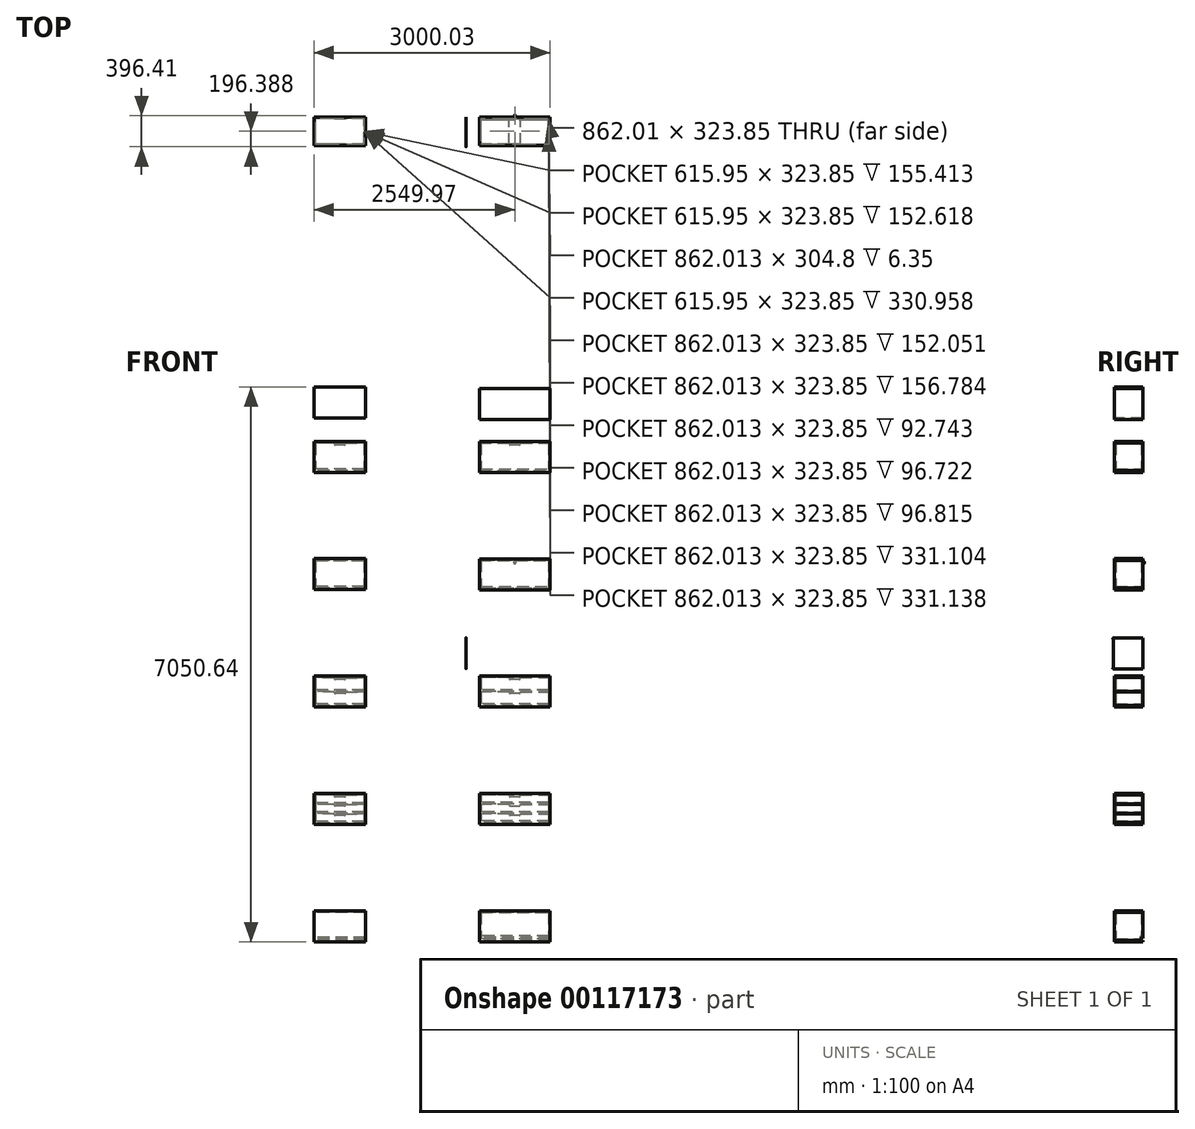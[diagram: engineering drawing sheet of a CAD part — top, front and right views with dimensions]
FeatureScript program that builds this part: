
annotation { "Feature Type Name" : "Feature", "Feature Type Description" : "" }
export const myFeature = defineFeature(function(context is Context, id is Id, definition is map)
    precondition{}
    {
        {
            var Q0;
            Q0=qCreatedBy(makeId("Front.planeOp"),FACE);
            var sketch = newSketch(context, id + "F0", { "sketchPlane" : qUnion([Q0])});
            skLineSegment(sketch, "E0", {"start": v(170.28, 4762.46) * mm, "end": v(167.36, 4762.46) * mm});
            skLineSegment(sketch, "E1", {"start": v(170.28, 4769.46) * mm, "end": v(167.36, 4769.46) * mm});
            skLineSegment(sketch, "E2", {"start": v(167.36, 4391.46) * mm, "end": v(170.28, 4391.46) * mm});
            skLineSegment(sketch, "E3", {"start": v(167.36, 4391.46) * mm, "end": v(167.36, 4769.46) * mm});
            skLineSegment(sketch, "E4", {"start": v(170.28, 4391.46) * mm, "end": v(170.28, 4769.46) * mm});
            skLineSegment(sketch, "E5", {"start": v(170.28, 3279.46) * mm, "end": v(167.36, 3279.46) * mm});
            skLineSegment(sketch, "E6", {"start": v(1435.25, 5048.46) * mm, "end": v(1435.25, 5411.54) * mm});
            skLineSegment(sketch, "E7", {"start": v(170.32, 5032.75) * mm, "end": v(170.32, 5427.25) * mm});
            skLineSegment(sketch, "E8", {"start": v(167.32, 5427.25) * mm, "end": v(167.32, 5032.75) * mm});
            skLineSegment(sketch, "E9", {"start": v(1070.32, 5032.75) * mm, "end": v(1070.32, 5427.25) * mm});
            skLineSegment(sketch, "E10", {"start": v(1073.32, 5427.25) * mm, "end": v(1073.32, 5032.75) * mm});
            skLineSegment(sketch, "E11", {"start": v(1809.25, 3937.25) * mm, "end": v(1809.25, 3542.75) * mm});
            skLineSegment(sketch, "E12", {"start": v(1809.25, 5427.25) * mm, "end": v(1809.25, 5032.75) * mm});
            skLineSegment(sketch, "E13", {"start": v(167.32, 3930.25) * mm, "end": v(170.32, 3930.25) * mm});
            skLineSegment(sketch, "E14", {"start": v(167.32, 5032.75) * mm, "end": v(170.32, 5032.75) * mm});
            skLineSegment(sketch, "E15", {"start": v(1073.32, 5032.75) * mm, "end": v(1070.32, 5032.75) * mm});
            skLineSegment(sketch, "E16", {"start": v(170.32, 5032.75) * mm, "end": v(1070.32, 5032.75) * mm});
            skLineSegment(sketch, "E17", {"start": v(1070.32, 5051.75) * mm, "end": v(170.32, 5051.75) * mm});
            skLineSegment(sketch, "E18", {"start": v(170.28, 4391.46) * mm, "end": v(1070.36, 4391.46) * mm});
            skLineSegment(sketch, "E19", {"start": v(170.28, 4747.46) * mm, "end": v(1070.36, 4747.46) * mm});
            skLineSegment(sketch, "E20", {"start": v(1073.28, 4391.46) * mm, "end": v(1070.36, 4391.46) * mm});
            skLineSegment(sketch, "E21", {"start": v(1073.28, 4391.46) * mm, "end": v(1073.28, 4769.46) * mm});
            skLineSegment(sketch, "E22", {"start": v(1070.36, 4391.46) * mm, "end": v(1070.36, 4769.46) * mm});
            skLineSegment(sketch, "E23", {"start": v(1070.36, 4769.46) * mm, "end": v(1073.28, 4769.46) * mm});
            skLineSegment(sketch, "E24", {"start": v(1070.36, 4762.46) * mm, "end": v(1073.28, 4762.46) * mm});
            skLineSegment(sketch, "E25", {"start": v(170.32, 3918.25) * mm, "end": v(1070.32, 3918.25) * mm});
            skLineSegment(sketch, "E26", {"start": v(1070.32, 3561.75) * mm, "end": v(170.32, 3561.75) * mm});
            skLineSegment(sketch, "E27", {"start": v(170.32, 3542.75) * mm, "end": v(1070.32, 3542.75) * mm});
            skLineSegment(sketch, "E28", {"start": v(170.32, 3937.25) * mm, "end": v(1070.32, 3937.25) * mm});
            skLineSegment(sketch, "E29", {"start": v(1073.32, 3937.25) * mm, "end": v(1073.32, 3542.75) * mm});
            skLineSegment(sketch, "E30", {"start": v(1070.32, 3542.75) * mm, "end": v(1070.32, 3937.25) * mm});
            skLineSegment(sketch, "E31", {"start": v(1073.32, 3542.75) * mm, "end": v(1070.32, 3542.75) * mm});
            skLineSegment(sketch, "E32", {"start": v(1073.32, 3937.25) * mm, "end": v(1070.32, 3937.25) * mm});
            skLineSegment(sketch, "E33", {"start": v(1073.32, 3930.25) * mm, "end": v(1070.32, 3930.25) * mm});
            skLineSegment(sketch, "E34", {"start": v(170.28, 3257.46) * mm, "end": v(1070.36, 3257.46) * mm});
            skLineSegment(sketch, "E35", {"start": v(1070.36, 3279.46) * mm, "end": v(1073.28, 3279.46) * mm});
            skLineSegment(sketch, "E36", {"start": v(1070.36, 3272.46) * mm, "end": v(1073.28, 3272.46) * mm});
            skLineSegment(sketch, "E37", {"start": v(170.28, 3272.46) * mm, "end": v(167.36, 3272.46) * mm});
            skLineSegment(sketch, "E38", {"start": v(1073.32, 5427.25) * mm, "end": v(1070.32, 5427.25) * mm});
            skLineSegment(sketch, "E39", {"start": v(170.32, 5427.25) * mm, "end": v(1070.32, 5427.25) * mm});
            skLineSegment(sketch, "E40", {"start": v(170.32, 5408.25) * mm, "end": v(1070.32, 5408.25) * mm});
            skCircle(sketch, "E41", {"center": v(1439.75, 5041.25) * mm, "radius": 4 * mm});
            skEllipticalArc(sketch, "E42", {});
            skCircle(sketch, "E43", {"center": v(1439.75, 3928.75) * mm, "radius": 4 * mm});
            skEllipticalArc(sketch, "E44", {});
            skCircle(sketch, "E45", {"center": v(1439.75, 3551.25) * mm, "radius": 4 * mm});
            skEllipticalArc(sketch, "E46", {});
            skLineSegment(sketch, "E47", {"start": v(1435.25, 3558.46) * mm, "end": v(1435.25, 3921.54) * mm});
            skCircle(sketch, "E48", {"center": v(620.36, 3888.25) * mm, "radius": 13 * mm});
            skCircle(sketch, "E49", {"center": v(620.36, 3888.25) * mm, "radius": 14 * mm});
            skLineSegment(sketch, "E50", {"start": v(621.1, 3893.25) * mm, "end": v(621.1, 3883.25) * mm});
            skLineSegment(sketch, "E51", {"start": v(621.1, 3883.25) * mm, "end": v(619.6, 3883.25) * mm});
            skLineSegment(sketch, "E52", {"start": v(619.6, 3883.25) * mm, "end": v(619.6, 3893.25) * mm});
            skLineSegment(sketch, "E53", {"start": v(621.1, 3893.25) * mm, "end": v(619.6, 3893.25) * mm});
            skLineSegment(sketch, "E54", {"start": v(170.32, 3542.75) * mm, "end": v(170.32, 3937.25) * mm});
            skLineSegment(sketch, "E55", {"start": v(167.32, 3937.25) * mm, "end": v(167.32, 3542.75) * mm});
            skLineSegment(sketch, "E56", {"start": v(167.32, 3542.75) * mm, "end": v(170.32, 3542.75) * mm});
            skLineSegment(sketch, "E57", {"start": v(167.32, 3937.25) * mm, "end": v(170.32, 3937.25) * mm});
            skLineSegment(sketch, "E58", {"start": v(170.28, 277.46) * mm, "end": v(1070.36, 277.46) * mm});
            skLineSegment(sketch, "E59", {"start": v(1070.36, 299.46) * mm, "end": v(1073.28, 299.46) * mm});
            skLineSegment(sketch, "E60", {"start": v(1070.36, 292.46) * mm, "end": v(1073.28, 292.46) * mm});
            skLineSegment(sketch, "E61", {"start": v(170.28, 292.46) * mm, "end": v(167.36, 292.46) * mm});
            skLineSegment(sketch, "E62", {"start": v(170.28, 1782.46) * mm, "end": v(167.36, 1782.46) * mm});
            skLineSegment(sketch, "E63", {"start": v(167.36, 1411.46) * mm, "end": v(170.28, 1411.46) * mm});
            skLineSegment(sketch, "E64", {"start": v(167.36, 1411.46) * mm, "end": v(167.36, 1789.46) * mm});
            skLineSegment(sketch, "E65", {"start": v(170.28, 1411.46) * mm, "end": v(170.28, 1789.46) * mm});
            skLineSegment(sketch, "E66", {"start": v(170.28, 299.46) * mm, "end": v(167.36, 299.46) * mm});
            skLineSegment(sketch, "E67", {"start": v(170.28, 1789.46) * mm, "end": v(167.36, 1789.46) * mm});
            skLineSegment(sketch, "E68", {"start": v(1809.25, 2447.25) * mm, "end": v(1809.25, 2052.75) * mm});
            skLineSegment(sketch, "E69", {"start": v(1809.25, 957.25) * mm, "end": v(1809.25, 562.75) * mm});
            skCircle(sketch, "E70", {"center": v(1439.75, 5418.75) * mm, "radius": 4 * mm});
            skEllipticalArc(sketch, "E71", {});
            skArc(sketch, "E72", {"start": v(548.59, 5408.25) * mm, "mid": v(550.53, 5407.44) * mm, "end": v(551.34, 5405.5) * mm});
            skLineSegment(sketch, "E73", {"start": v(560.34, 5382.25) * mm, "end": v(680.34, 5382.25) * mm});
            skArc(sketch, "E74", {"start": v(551.34, 5391.25) * mm, "mid": v(553.97, 5384.88) * mm, "end": v(560.34, 5382.25) * mm});
            skArc(sketch, "E75", {"start": v(680.34, 5382.25) * mm, "mid": v(686.7, 5384.88) * mm, "end": v(689.34, 5391.25) * mm});
            skArc(sketch, "E76", {"start": v(692.09, 5408.25) * mm, "mid": v(690.14, 5407.44) * mm, "end": v(689.34, 5405.5) * mm});
            skLineSegment(sketch, "E77", {"start": v(551.34, 5405.5) * mm, "end": v(551.34, 5391.25) * mm});
            skLineSegment(sketch, "E78", {"start": v(689.34, 5405.5) * mm, "end": v(689.34, 5391.25) * mm});
            skLineSegment(sketch, "E79", {"start": v(167.32, 5427.25) * mm, "end": v(170.32, 5427.25) * mm});
            skLineSegment(sketch, "E80", {"start": v(167.32, 5420.25) * mm, "end": v(170.32, 5420.25) * mm});
            skLineSegment(sketch, "E81", {"start": v(1073.32, 5420.25) * mm, "end": v(1070.32, 5420.25) * mm});
            skLineSegment(sketch, "E82", {"start": v(170.32, 2447.25) * mm, "end": v(1070.32, 2447.25) * mm});
            skLineSegment(sketch, "E83", {"start": v(170.32, 2250) * mm, "end": v(1070.32, 2250) * mm});
            skLineSegment(sketch, "E84", {"start": v(1073.32, 2447.25) * mm, "end": v(1073.32, 2052.75) * mm});
            skLineSegment(sketch, "E85", {"start": v(1070.32, 2052.75) * mm, "end": v(1070.32, 2447.25) * mm});
            skLineSegment(sketch, "E86", {"start": v(1073.32, 2052.75) * mm, "end": v(1070.32, 2052.75) * mm});
            skLineSegment(sketch, "E87", {"start": v(1073.32, 2447.25) * mm, "end": v(1070.32, 2447.25) * mm});
            skLineSegment(sketch, "E88", {"start": v(1073.32, 2440.25) * mm, "end": v(1070.32, 2440.25) * mm});
            skLineSegment(sketch, "E89", {"start": v(170.28, 1767.46) * mm, "end": v(1070.36, 1767.46) * mm});
            skLineSegment(sketch, "E90", {"start": v(170.28, 1411.46) * mm, "end": v(1070.36, 1411.46) * mm});
            skLineSegment(sketch, "E91", {"start": v(1073.28, 1411.46) * mm, "end": v(1073.28, 1789.46) * mm});
            skLineSegment(sketch, "E92", {"start": v(1070.36, 1411.46) * mm, "end": v(1070.36, 1789.46) * mm});
            skLineSegment(sketch, "E93", {"start": v(1073.28, 1411.46) * mm, "end": v(1070.36, 1411.46) * mm});
            skLineSegment(sketch, "E94", {"start": v(1070.36, 1789.46) * mm, "end": v(1073.28, 1789.46) * mm});
            skLineSegment(sketch, "E95", {"start": v(1070.36, 1782.46) * mm, "end": v(1073.28, 1782.46) * mm});
            skLineSegment(sketch, "E96", {"start": v(170.32, 957.25) * mm, "end": v(1070.32, 957.25) * mm});
            skLineSegment(sketch, "E97", {"start": v(170.32, 938.25) * mm, "end": v(1070.32, 938.25) * mm});
            skLineSegment(sketch, "E98", {"start": v(1070.32, 581.75) * mm, "end": v(170.32, 581.75) * mm});
            skLineSegment(sketch, "E99", {"start": v(170.32, 562.75) * mm, "end": v(1070.32, 562.75) * mm});
            skLineSegment(sketch, "E100", {"start": v(170.32, 700.58) * mm, "end": v(1070.32, 700.58) * mm});
            skLineSegment(sketch, "E101", {"start": v(170.32, 819.4) * mm, "end": v(1070.32, 819.4) * mm});
            skLineSegment(sketch, "E102", {"start": v(1073.32, 957.25) * mm, "end": v(1070.32, 957.25) * mm});
            skLineSegment(sketch, "E103", {"start": v(1073.32, 957.25) * mm, "end": v(1073.32, 562.75) * mm});
            skLineSegment(sketch, "E104", {"start": v(1070.32, 562.75) * mm, "end": v(1070.32, 957.25) * mm});
            skLineSegment(sketch, "E105", {"start": v(1073.32, 562.75) * mm, "end": v(1070.32, 562.75) * mm});
            skLineSegment(sketch, "E106", {"start": v(1073.32, 950.25) * mm, "end": v(1070.32, 950.25) * mm});
            skArc(sketch, "E107", {"start": v(692.09, 2250) * mm, "mid": v(690.14, 2249.2) * mm, "end": v(689.34, 2247.25) * mm});
            skLineSegment(sketch, "E108", {"start": v(551.34, 2247.25) * mm, "end": v(551.34, 2233) * mm});
            skLineSegment(sketch, "E109", {"start": v(689.34, 2247.25) * mm, "end": v(689.34, 2233) * mm});
            skArc(sketch, "E110", {"start": v(548.59, 2250) * mm, "mid": v(550.53, 2249.2) * mm, "end": v(551.34, 2247.25) * mm});
            skArc(sketch, "E111", {"start": v(680.34, 2224) * mm, "mid": v(686.7, 2226.63) * mm, "end": v(689.34, 2233) * mm});
            skArc(sketch, "E112", {"start": v(692.09, 938.25) * mm, "mid": v(690.14, 937.44) * mm, "end": v(689.34, 935.5) * mm});
            skLineSegment(sketch, "E113", {"start": v(560.34, 912.25) * mm, "end": v(680.34, 912.25) * mm});
            skArc(sketch, "E114", {"start": v(680.34, 912.25) * mm, "mid": v(686.7, 914.88) * mm, "end": v(689.34, 921.25) * mm});
            skArc(sketch, "E115", {"start": v(551.34, 921.25) * mm, "mid": v(553.97, 914.88) * mm, "end": v(560.34, 912.25) * mm});
            skArc(sketch, "E116", {"start": v(692.09, 819.4) * mm, "mid": v(690.14, 818.6) * mm, "end": v(689.34, 816.66) * mm});
            skArc(sketch, "E117", {"start": v(548.59, 700.58) * mm, "mid": v(550.53, 699.77) * mm, "end": v(551.34, 697.83) * mm});
            skLineSegment(sketch, "E118", {"start": v(689.34, 697.83) * mm, "end": v(689.34, 683.58) * mm});
            skLineSegment(sketch, "E119", {"start": v(170.32, 562.75) * mm, "end": v(170.32, 957.25) * mm});
            skLineSegment(sketch, "E120", {"start": v(167.32, 957.25) * mm, "end": v(167.32, 562.75) * mm});
            skLineSegment(sketch, "E121", {"start": v(167.32, 562.75) * mm, "end": v(170.32, 562.75) * mm});
            skLineSegment(sketch, "E122", {"start": v(167.32, 957.25) * mm, "end": v(170.32, 957.25) * mm});
            skLineSegment(sketch, "E123", {"start": v(167.32, 950.25) * mm, "end": v(170.32, 950.25) * mm});
            skLineSegment(sketch, "E124", {"start": v(170.32, 2052.75) * mm, "end": v(170.32, 2447.25) * mm});
            skLineSegment(sketch, "E125", {"start": v(167.32, 2447.25) * mm, "end": v(167.32, 2052.75) * mm});
            skLineSegment(sketch, "E126", {"start": v(167.32, 2052.75) * mm, "end": v(170.32, 2052.75) * mm});
            skLineSegment(sketch, "E127", {"start": v(167.32, 2447.25) * mm, "end": v(170.32, 2447.25) * mm});
            skLineSegment(sketch, "E128", {"start": v(167.32, 2440.25) * mm, "end": v(170.32, 2440.25) * mm});
            skLineSegment(sketch, "E129", {"start": v(170.32, 2428.25) * mm, "end": v(1070.32, 2428.25) * mm});
            skLineSegment(sketch, "E130", {"start": v(1070.32, 2071.75) * mm, "end": v(170.32, 2071.75) * mm});
            skLineSegment(sketch, "E131", {"start": v(170.32, 2052.75) * mm, "end": v(1070.32, 2052.75) * mm});
            skEllipticalArc(sketch, "E132", {});
            skLineSegment(sketch, "E133", {"start": v(1435.25, 578.46) * mm, "end": v(1435.25, 941.54) * mm});
            skLineSegment(sketch, "E134", {"start": v(551.34, 816.66) * mm, "end": v(551.34, 802.4) * mm});
            skArc(sketch, "E135", {"start": v(548.59, 938.25) * mm, "mid": v(550.53, 937.44) * mm, "end": v(551.34, 935.5) * mm});
            skLineSegment(sketch, "E136", {"start": v(689.34, 935.5) * mm, "end": v(689.34, 921.25) * mm});
            skLineSegment(sketch, "E137", {"start": v(551.34, 935.5) * mm, "end": v(551.34, 921.25) * mm});
            skLineSegment(sketch, "E138", {"start": v(551.34, 697.83) * mm, "end": v(551.34, 683.58) * mm});
            skArc(sketch, "E139", {"start": v(692.09, 700.58) * mm, "mid": v(690.14, 699.77) * mm, "end": v(689.34, 697.83) * mm});
            skLineSegment(sketch, "E140", {"start": v(560.34, 674.58) * mm, "end": v(680.34, 674.58) * mm});
            skArc(sketch, "E141", {"start": v(680.34, 674.58) * mm, "mid": v(686.7, 677.21) * mm, "end": v(689.34, 683.58) * mm});
            skArc(sketch, "E142", {"start": v(551.34, 683.58) * mm, "mid": v(553.97, 677.21) * mm, "end": v(560.34, 674.58) * mm});
            skArc(sketch, "E143", {"start": v(551.34, 802.4) * mm, "mid": v(553.97, 796.04) * mm, "end": v(560.34, 793.4) * mm});
            skArc(sketch, "E144", {"start": v(680.34, 793.4) * mm, "mid": v(686.7, 796.04) * mm, "end": v(689.34, 802.4) * mm});
            skLineSegment(sketch, "E145", {"start": v(560.34, 793.4) * mm, "end": v(680.34, 793.4) * mm});
            skLineSegment(sketch, "E146", {"start": v(689.34, 816.66) * mm, "end": v(689.34, 802.4) * mm});
            skArc(sketch, "E147", {"start": v(548.59, 819.4) * mm, "mid": v(550.53, 818.6) * mm, "end": v(551.34, 816.66) * mm});
            skArc(sketch, "E148", {"start": v(548.59, 2428.25) * mm, "mid": v(550.53, 2427.44) * mm, "end": v(551.34, 2425.5) * mm});
            skLineSegment(sketch, "E149", {"start": v(689.34, 2425.5) * mm, "end": v(689.34, 2411.25) * mm});
            skLineSegment(sketch, "E150", {"start": v(551.34, 2425.5) * mm, "end": v(551.34, 2411.25) * mm});
            skArc(sketch, "E151", {"start": v(692.09, 2428.25) * mm, "mid": v(690.14, 2427.44) * mm, "end": v(689.34, 2425.5) * mm});
            skLineSegment(sketch, "E152", {"start": v(560.34, 2402.25) * mm, "end": v(680.34, 2402.25) * mm});
            skArc(sketch, "E153", {"start": v(680.34, 2402.25) * mm, "mid": v(686.7, 2404.88) * mm, "end": v(689.34, 2411.25) * mm});
            skArc(sketch, "E154", {"start": v(551.34, 2411.25) * mm, "mid": v(553.97, 2404.88) * mm, "end": v(560.34, 2402.25) * mm});
            skArc(sketch, "E155", {"start": v(551.34, 2233) * mm, "mid": v(553.97, 2226.63) * mm, "end": v(560.34, 2224) * mm});
            skLineSegment(sketch, "E156", {"start": v(560.34, 2224) * mm, "end": v(680.34, 2224) * mm});
            skLineSegment(sketch, "E157", {"start": v(-1274.6, 4769.46) * mm, "end": v(-1271.68, 4769.46) * mm});
            skLineSegment(sketch, "E158", {"start": v(-1271.68, 4391.46) * mm, "end": v(-1274.6, 4391.46) * mm});
            skLineSegment(sketch, "E159", {"start": v(-1274.6, 4391.46) * mm, "end": v(-1274.6, 4769.46) * mm});
            skLineSegment(sketch, "E160", {"start": v(-1271.68, 4391.46) * mm, "end": v(-1271.68, 4769.46) * mm});
            skLineSegment(sketch, "E161", {"start": v(-1274.6, 4762.46) * mm, "end": v(-1271.68, 4762.46) * mm});
            skLineSegment(sketch, "E162", {"start": v(-1274.6, 3279.46) * mm, "end": v(-1271.68, 3279.46) * mm});
            skLineSegment(sketch, "E163", {"start": v(-1274.6, 3272.46) * mm, "end": v(-1271.68, 3272.46) * mm});
            skLineSegment(sketch, "E164", {"start": v(-664.75, 5048.46) * mm, "end": v(-664.75, 5411.54) * mm});
            skLineSegment(sketch, "E165", {"start": v(-290.75, 5427.25) * mm, "end": v(-290.75, 5032.75) * mm});
            skLineSegment(sketch, "E166", {"start": v(-1271.64, 5427.25) * mm, "end": v(-1271.64, 5032.75) * mm});
            skLineSegment(sketch, "E167", {"start": v(-1274.64, 5032.75) * mm, "end": v(-1274.64, 5427.25) * mm});
            skCircle(sketch, "E168", {"center": v(1439.75, 2438.75) * mm, "radius": 4 * mm});
            skEllipticalArc(sketch, "E169", {});
            skCircle(sketch, "E170", {"center": v(1439.75, 2061.25) * mm, "radius": 4 * mm});
            skEllipticalArc(sketch, "E171", {});
            skLineSegment(sketch, "E172", {"start": v(1435.25, 2068.46) * mm, "end": v(1435.25, 2431.54) * mm});
            skCircle(sketch, "E173", {"center": v(1439.75, 948.75) * mm, "radius": 4 * mm});
            skEllipticalArc(sketch, "E174", {});
            skCircle(sketch, "E175", {"center": v(1439.75, 571.25) * mm, "radius": 4 * mm});
            skLineSegment(sketch, "E176", {"start": v(-1929.64, 5032.75) * mm, "end": v(-1929.64, 5427.25) * mm});
            skLineSegment(sketch, "E177", {"start": v(-1271.64, 5420.25) * mm, "end": v(-1274.64, 5420.25) * mm});
            skLineSegment(sketch, "E178", {"start": v(-660.25, 5427.25) * mm, "end": v(-290.75, 5427.25) * mm});
            skCircle(sketch, "E179", {"center": v(-660.25, 5418.75) * mm, "radius": 4 * mm});
            skEllipticalArc(sketch, "E180", {});
            skLineSegment(sketch, "E181", {"start": v(-1271.64, 5427.25) * mm, "end": v(-1274.64, 5427.25) * mm});
            skLineSegment(sketch, "E182", {"start": v(-1271.64, 3930.25) * mm, "end": v(-1274.64, 3930.25) * mm});
            skCircle(sketch, "E183", {"center": v(-660.25, 5041.25) * mm, "radius": 4 * mm});
            skEllipticalArc(sketch, "E184", {});
            skLineSegment(sketch, "E185", {"start": v(-660.61, 5032.75) * mm, "end": v(-290.75, 5032.75) * mm});
            skCircle(sketch, "E186", {"center": v(-660.25, 3928.75) * mm, "radius": 4 * mm});
            skEllipticalArc(sketch, "E187", {});
            skLineSegment(sketch, "E188", {"start": v(-660.25, 3937.25) * mm, "end": v(-290.75, 3937.25) * mm});
            skCircle(sketch, "E189", {"center": v(-660.25, 3551.25) * mm, "radius": 4 * mm});
            skEllipticalArc(sketch, "E190", {});
            skLineSegment(sketch, "E191", {"start": v(-660.61, 3542.75) * mm, "end": v(-290.75, 3542.75) * mm});
            skLineSegment(sketch, "E192", {"start": v(-664.75, 3558.46) * mm, "end": v(-664.75, 3921.54) * mm});
            skLineSegment(sketch, "E193", {"start": v(-290.75, 3937.25) * mm, "end": v(-290.75, 3542.75) * mm});
            skLineSegment(sketch, "E194", {"start": v(-1274.64, 3542.75) * mm, "end": v(-1274.64, 3937.25) * mm});
            skLineSegment(sketch, "E195", {"start": v(-1271.64, 3542.75) * mm, "end": v(-1274.64, 3542.75) * mm});
            skLineSegment(sketch, "E196", {"start": v(-1271.64, 3937.25) * mm, "end": v(-1274.64, 3937.25) * mm});
            skLineSegment(sketch, "E197", {"start": v(-1271.64, 3937.25) * mm, "end": v(-1271.64, 3542.75) * mm});
            skLineSegment(sketch, "E198", {"start": v(-1271.64, 5032.75) * mm, "end": v(-1274.64, 5032.75) * mm});
            skLineSegment(sketch, "E199", {"start": v(-1671.16, 5405.5) * mm, "end": v(-1671.16, 5391.25) * mm});
            skLineSegment(sketch, "E200", {"start": v(-1932.64, 3930.25) * mm, "end": v(-1929.64, 3930.25) * mm});
            skLineSegment(sketch, "E201", {"start": v(-1932.64, 5032.75) * mm, "end": v(-1929.64, 5032.75) * mm});
            skLineSegment(sketch, "E202", {"start": v(-1932.64, 3937.25) * mm, "end": v(-1929.64, 3937.25) * mm});
            skLineSegment(sketch, "E203", {"start": v(-1932.64, 3542.75) * mm, "end": v(-1929.64, 3542.75) * mm});
            skLineSegment(sketch, "E204", {"start": v(-1932.64, 3937.25) * mm, "end": v(-1932.64, 3542.75) * mm});
            skLineSegment(sketch, "E205", {"start": v(-1929.64, 3542.75) * mm, "end": v(-1929.64, 3937.25) * mm});
            skLineSegment(sketch, "E206", {"start": v(-1929.68, 3279.46) * mm, "end": v(-1932.6, 3279.46) * mm});
            skLineSegment(sketch, "E207", {"start": v(-1929.68, 3272.46) * mm, "end": v(-1932.6, 3272.46) * mm});
            skLineSegment(sketch, "E208", {"start": v(-1929.68, 4391.46) * mm, "end": v(-1929.68, 4769.46) * mm});
            skLineSegment(sketch, "E209", {"start": v(-1932.6, 4391.46) * mm, "end": v(-1932.6, 4769.46) * mm});
            skLineSegment(sketch, "E210", {"start": v(-1932.6, 4391.46) * mm, "end": v(-1929.68, 4391.46) * mm});
            skLineSegment(sketch, "E211", {"start": v(-1929.68, 4769.46) * mm, "end": v(-1932.6, 4769.46) * mm});
            skLineSegment(sketch, "E212", {"start": v(-1929.68, 4762.46) * mm, "end": v(-1932.6, 4762.46) * mm});
            skCircle(sketch, "E213", {"center": v(-1602.14, 3888.25) * mm, "radius": 13 * mm});
            skCircle(sketch, "E214", {"center": v(-1602.14, 3888.25) * mm, "radius": 14 * mm});
            skLineSegment(sketch, "E215", {"start": v(-1602.9, 3883.25) * mm, "end": v(-1602.9, 3893.25) * mm});
            skLineSegment(sketch, "E216", {"start": v(-1601.4, 3893.25) * mm, "end": v(-1602.9, 3893.25) * mm});
            skLineSegment(sketch, "E217", {"start": v(-1601.4, 3883.25) * mm, "end": v(-1602.9, 3883.25) * mm});
            skLineSegment(sketch, "E218", {"start": v(-1601.4, 3893.25) * mm, "end": v(-1601.4, 3883.25) * mm});
            skLineSegment(sketch, "E219", {"start": v(-1932.64, 5427.25) * mm, "end": v(-1932.64, 5032.75) * mm});
            skLineSegment(sketch, "E220", {"start": v(-660.61, 562.75) * mm, "end": v(-290.75, 562.75) * mm});
            skLineSegment(sketch, "E221", {"start": v(-664.75, 578.46) * mm, "end": v(-664.75, 941.54) * mm});
            skLineSegment(sketch, "E222", {"start": v(-290.75, 957.25) * mm, "end": v(-290.75, 562.75) * mm});
            skCircle(sketch, "E223", {"center": v(-660.25, 948.75) * mm, "radius": 4 * mm});
            skCircle(sketch, "E224", {"center": v(-660.25, 2438.75) * mm, "radius": 4 * mm});
            skEllipticalArc(sketch, "E225", {});
            skLineSegment(sketch, "E226", {"start": v(-1271.64, 957.25) * mm, "end": v(-1271.64, 562.75) * mm});
            skLineSegment(sketch, "E227", {"start": v(-1274.64, 562.75) * mm, "end": v(-1274.64, 957.25) * mm});
            skLineSegment(sketch, "E228", {"start": v(-1271.64, 562.75) * mm, "end": v(-1274.64, 562.75) * mm});
            skLineSegment(sketch, "E229", {"start": v(-1271.64, 957.25) * mm, "end": v(-1274.64, 957.25) * mm});
            skLineSegment(sketch, "E230", {"start": v(-1271.64, 2447.25) * mm, "end": v(-1274.64, 2447.25) * mm});
            skLineSegment(sketch, "E231", {"start": v(-1271.64, 2447.25) * mm, "end": v(-1271.64, 2052.75) * mm});
            skLineSegment(sketch, "E232", {"start": v(-1274.64, 2052.75) * mm, "end": v(-1274.64, 2447.25) * mm});
            skLineSegment(sketch, "E233", {"start": v(-1271.64, 2052.75) * mm, "end": v(-1274.64, 2052.75) * mm});
            skLineSegment(sketch, "E234", {"start": v(-1274.6, 1789.46) * mm, "end": v(-1271.68, 1789.46) * mm});
            skLineSegment(sketch, "E235", {"start": v(-1271.68, 1411.46) * mm, "end": v(-1274.6, 1411.46) * mm});
            skLineSegment(sketch, "E236", {"start": v(-1274.6, 1411.46) * mm, "end": v(-1274.6, 1789.46) * mm});
            skLineSegment(sketch, "E237", {"start": v(-1271.68, 1411.46) * mm, "end": v(-1271.68, 1789.46) * mm});
            skLineSegment(sketch, "E238", {"start": v(-1274.6, 1782.46) * mm, "end": v(-1271.68, 1782.46) * mm});
            skLineSegment(sketch, "E239", {"start": v(-1274.6, 299.46) * mm, "end": v(-1271.68, 299.46) * mm});
            skLineSegment(sketch, "E240", {"start": v(-1274.6, 292.46) * mm, "end": v(-1271.68, 292.46) * mm});
            skLineSegment(sketch, "E241", {"start": v(-1932.64, 5420.25) * mm, "end": v(-1929.64, 5420.25) * mm});
            skLineSegment(sketch, "E242", {"start": v(-1932.64, 5427.25) * mm, "end": v(-1929.64, 5427.25) * mm});
            skArc(sketch, "E243", {"start": v(-1671.16, 5391.25) * mm, "mid": v(-1668.53, 5384.88) * mm, "end": v(-1662.16, 5382.25) * mm});
            skArc(sketch, "E244", {"start": v(-1673.91, 5408.25) * mm, "mid": v(-1671.97, 5407.44) * mm, "end": v(-1671.16, 5405.5) * mm});
            skArc(sketch, "E245", {"start": v(-1671.16, 802.4) * mm, "mid": v(-1668.53, 796.04) * mm, "end": v(-1662.16, 793.4) * mm});
            skArc(sketch, "E246", {"start": v(-1671.16, 683.58) * mm, "mid": v(-1668.53, 677.21) * mm, "end": v(-1662.16, 674.58) * mm});
            skArc(sketch, "E247", {"start": v(-1671.16, 2233) * mm, "mid": v(-1668.53, 2226.63) * mm, "end": v(-1662.16, 2224) * mm});
            skArc(sketch, "E248", {"start": v(-1671.16, 2411.25) * mm, "mid": v(-1668.53, 2404.88) * mm, "end": v(-1662.16, 2402.25) * mm});
            skLineSegment(sketch, "E249", {"start": v(-1929.68, 299.46) * mm, "end": v(-1932.6, 299.46) * mm});
            skLineSegment(sketch, "E250", {"start": v(-1929.68, 292.46) * mm, "end": v(-1932.6, 292.46) * mm});
            skLineSegment(sketch, "E251", {"start": v(-1932.6, 1411.46) * mm, "end": v(-1932.6, 1789.46) * mm});
            skLineSegment(sketch, "E252", {"start": v(-1929.68, 1411.46) * mm, "end": v(-1929.68, 1789.46) * mm});
            skLineSegment(sketch, "E253", {"start": v(-1929.68, 1789.46) * mm, "end": v(-1932.6, 1789.46) * mm});
            skLineSegment(sketch, "E254", {"start": v(-1932.6, 1411.46) * mm, "end": v(-1929.68, 1411.46) * mm});
            skLineSegment(sketch, "E255", {"start": v(-1929.68, 1782.46) * mm, "end": v(-1932.6, 1782.46) * mm});
            skLineSegment(sketch, "E256", {"start": v(-1271.64, 2440.25) * mm, "end": v(-1274.64, 2440.25) * mm});
            skLineSegment(sketch, "E257", {"start": v(-1271.64, 950.25) * mm, "end": v(-1274.64, 950.25) * mm});
            skLineSegment(sketch, "E258", {"start": v(-660.25, 2447.25) * mm, "end": v(-290.75, 2447.25) * mm});
            skCircle(sketch, "E259", {"center": v(-660.25, 2061.25) * mm, "radius": 4 * mm});
            skEllipticalArc(sketch, "E260", {});
            skLineSegment(sketch, "E261", {"start": v(-660.61, 2052.75) * mm, "end": v(-290.75, 2052.75) * mm});
            skLineSegment(sketch, "E262", {"start": v(-664.75, 2068.46) * mm, "end": v(-664.75, 2431.54) * mm});
            skLineSegment(sketch, "E263", {"start": v(-290.75, 2447.25) * mm, "end": v(-290.75, 2052.75) * mm});
            skEllipticalArc(sketch, "E264", {});
            skLineSegment(sketch, "E265", {"start": v(-660.25, 957.25) * mm, "end": v(-290.75, 957.25) * mm});
            skCircle(sketch, "E266", {"center": v(-660.25, 571.25) * mm, "radius": 4 * mm});
            skEllipticalArc(sketch, "E267", {});
            skLineSegment(sketch, "E268", {"start": v(-1932.64, 2440.25) * mm, "end": v(-1929.64, 2440.25) * mm});
            skLineSegment(sketch, "E269", {"start": v(-1932.64, 950.25) * mm, "end": v(-1929.64, 950.25) * mm});
            skLineSegment(sketch, "E270", {"start": v(-1932.64, 2447.25) * mm, "end": v(-1929.64, 2447.25) * mm});
            skLineSegment(sketch, "E271", {"start": v(-1932.64, 2052.75) * mm, "end": v(-1929.64, 2052.75) * mm});
            skLineSegment(sketch, "E272", {"start": v(-1932.64, 2447.25) * mm, "end": v(-1932.64, 2052.75) * mm});
            skLineSegment(sketch, "E273", {"start": v(-1929.64, 2052.75) * mm, "end": v(-1929.64, 2447.25) * mm});
            skLineSegment(sketch, "E274", {"start": v(-1932.64, 957.25) * mm, "end": v(-1929.64, 957.25) * mm});
            skLineSegment(sketch, "E275", {"start": v(-1932.64, 562.75) * mm, "end": v(-1929.64, 562.75) * mm});
            skLineSegment(sketch, "E276", {"start": v(-1932.64, 957.25) * mm, "end": v(-1932.64, 562.75) * mm});
            skLineSegment(sketch, "E277", {"start": v(-1929.64, 562.75) * mm, "end": v(-1929.64, 957.25) * mm});
            skLineSegment(sketch, "E278", {"start": v(-1671.16, 697.83) * mm, "end": v(-1671.16, 683.58) * mm});
            skArc(sketch, "E279", {"start": v(-1673.91, 700.58) * mm, "mid": v(-1671.97, 699.77) * mm, "end": v(-1671.16, 697.83) * mm});
            skArc(sketch, "E280", {"start": v(-1671.16, 921.25) * mm, "mid": v(-1668.53, 914.88) * mm, "end": v(-1662.16, 912.25) * mm});
            skLineSegment(sketch, "E281", {"start": v(-1671.16, 935.5) * mm, "end": v(-1671.16, 921.25) * mm});
            skArc(sketch, "E282", {"start": v(-1673.91, 938.25) * mm, "mid": v(-1671.97, 937.44) * mm, "end": v(-1671.16, 935.5) * mm});
            skArc(sketch, "E283", {"start": v(-1673.91, 819.4) * mm, "mid": v(-1671.97, 818.6) * mm, "end": v(-1671.16, 816.66) * mm});
            skLineSegment(sketch, "E284", {"start": v(-1671.16, 816.66) * mm, "end": v(-1671.16, 802.4) * mm});
            skArc(sketch, "E285", {"start": v(-1673.91, 2250) * mm, "mid": v(-1671.97, 2249.2) * mm, "end": v(-1671.16, 2247.25) * mm});
            skLineSegment(sketch, "E286", {"start": v(-1671.16, 2247.25) * mm, "end": v(-1671.16, 2233) * mm});
            skLineSegment(sketch, "E287", {"start": v(-1671.16, 2425.5) * mm, "end": v(-1671.16, 2411.25) * mm});
            skArc(sketch, "E288", {"start": v(-1673.91, 2428.25) * mm, "mid": v(-1671.97, 2427.44) * mm, "end": v(-1671.16, 2425.5) * mm});
            skLineSegment(sketch, "E289", {"start": v(167.36, -1568.54) * mm, "end": v(167.36, -1190.54) * mm});
            skLineSegment(sketch, "E290", {"start": v(170.28, -1568.54) * mm, "end": v(170.28, -1190.54) * mm});
            skLineSegment(sketch, "E291", {"start": v(167.36, -78.54) * mm, "end": v(170.28, -78.54) * mm});
            skCircle(sketch, "E292", {"center": v(1439.75, -2408.75) * mm, "radius": 4 * mm});
            skEllipticalArc(sketch, "E293", {});
            skLineSegment(sketch, "E294", {"start": v(1435.25, -2401.54) * mm, "end": v(1435.25, -2038.46) * mm});
            skLineSegment(sketch, "E295", {"start": v(170.32, -2417.25) * mm, "end": v(170.32, -2022.75) * mm});
            skLineSegment(sketch, "E296", {"start": v(167.32, -2022.75) * mm, "end": v(167.32, -2417.25) * mm});
            skLineSegment(sketch, "E297", {"start": v(167.32, -2417.25) * mm, "end": v(170.32, -2417.25) * mm});
            skLineSegment(sketch, "E298", {"start": v(1070.36, -2398.25) * mm, "end": v(170.32, -2398.25) * mm});
            skLineSegment(sketch, "E299", {"start": v(170.32, -2417.25) * mm, "end": v(1070.36, -2417.25) * mm});
            skLineSegment(sketch, "E300", {"start": v(1073.36, -2022.75) * mm, "end": v(1073.36, -2417.25) * mm});
            skLineSegment(sketch, "E301", {"start": v(1070.36, -2417.25) * mm, "end": v(1070.36, -2022.75) * mm});
            skLineSegment(sketch, "E302", {"start": v(1073.36, -2417.25) * mm, "end": v(1070.36, -2417.25) * mm});
            skLineSegment(sketch, "E303", {"start": v(170.28, -2702.54) * mm, "end": v(1070.36, -2702.54) * mm});
            skLineSegment(sketch, "E304", {"start": v(1070.36, -2680.54) * mm, "end": v(1073.28, -2680.54) * mm});
            skLineSegment(sketch, "E305", {"start": v(1070.36, -2687.54) * mm, "end": v(1073.28, -2687.54) * mm});
            skLineSegment(sketch, "E306", {"start": v(170.28, -2687.54) * mm, "end": v(167.36, -2687.54) * mm});
            skLineSegment(sketch, "E307", {"start": v(170.28, -2680.54) * mm, "end": v(167.36, -2680.54) * mm});
            skLineSegment(sketch, "E308", {"start": v(1809.25, -532.75) * mm, "end": v(1809.25, -927.25) * mm});
            skLineSegment(sketch, "E309", {"start": v(1809.25, -2022.75) * mm, "end": v(1809.25, -2417.25) * mm});
            skLineSegment(sketch, "E310", {"start": v(1073.28, -78.54) * mm, "end": v(1070.36, -78.54) * mm});
            skLineSegment(sketch, "E311", {"start": v(170.32, -878.25) * mm, "end": v(1070.32, -878.25) * mm});
            skLineSegment(sketch, "E312", {"start": v(1070.32, -908.25) * mm, "end": v(170.32, -908.25) * mm});
            skLineSegment(sketch, "E313", {"start": v(170.32, -927.25) * mm, "end": v(1070.32, -927.25) * mm});
            skLineSegment(sketch, "E314", {"start": v(170.32, -532.75) * mm, "end": v(1070.32, -532.75) * mm});
            skLineSegment(sketch, "E315", {"start": v(170.32, -551.75) * mm, "end": v(1070.32, -551.75) * mm});
            skLineSegment(sketch, "E316", {"start": v(1070.32, -927.25) * mm, "end": v(1070.32, -532.75) * mm});
            skLineSegment(sketch, "E317", {"start": v(1073.32, -927.25) * mm, "end": v(1070.32, -927.25) * mm});
            skLineSegment(sketch, "E318", {"start": v(1073.32, -532.75) * mm, "end": v(1070.32, -532.75) * mm});
            skLineSegment(sketch, "E319", {"start": v(1073.32, -532.75) * mm, "end": v(1073.32, -927.25) * mm});
            skLineSegment(sketch, "E320", {"start": v(1073.32, -539.75) * mm, "end": v(1070.32, -539.75) * mm});
            skLineSegment(sketch, "E321", {"start": v(170.28, -1212.54) * mm, "end": v(1070.36, -1212.54) * mm});
            skLineSegment(sketch, "E322", {"start": v(170.28, -1568.54) * mm, "end": v(1070.36, -1568.54) * mm});
            skLineSegment(sketch, "E323", {"start": v(1073.28, -1568.54) * mm, "end": v(1073.28, -1190.54) * mm});
            skLineSegment(sketch, "E324", {"start": v(1070.36, -1568.54) * mm, "end": v(1070.36, -1190.54) * mm});
            skLineSegment(sketch, "E325", {"start": v(1073.28, -1568.54) * mm, "end": v(1070.36, -1568.54) * mm});
            skLineSegment(sketch, "E326", {"start": v(1070.36, -1190.54) * mm, "end": v(1073.28, -1190.54) * mm});
            skLineSegment(sketch, "E327", {"start": v(1070.36, -1197.54) * mm, "end": v(1073.28, -1197.54) * mm});
            skLineSegment(sketch, "E328", {"start": v(170.32, -2041.75) * mm, "end": v(1070.36, -2041.75) * mm});
            skLineSegment(sketch, "E329", {"start": v(170.32, -2022.75) * mm, "end": v(1070.36, -2022.75) * mm});
            skLineSegment(sketch, "E330", {"start": v(1073.36, -2022.75) * mm, "end": v(1070.36, -2022.75) * mm});
            skLineSegment(sketch, "E331", {"start": v(1073.36, -2029.75) * mm, "end": v(1070.36, -2029.75) * mm});
            skLineSegment(sketch, "E332", {"start": v(170.28, -1197.54) * mm, "end": v(167.36, -1197.54) * mm});
            skLineSegment(sketch, "E333", {"start": v(170.28, -1190.54) * mm, "end": v(167.36, -1190.54) * mm});
            skLineSegment(sketch, "E334", {"start": v(167.36, -1568.54) * mm, "end": v(170.28, -1568.54) * mm});
            skCircle(sketch, "E335", {"center": v(620.36, -2071.75) * mm, "radius": 13 * mm});
            skCircle(sketch, "E336", {"center": v(620.36, -2071.75) * mm, "radius": 14 * mm});
            skCircle(sketch, "E337", {"center": v(1439.75, -541.25) * mm, "radius": 4 * mm});
            skEllipticalArc(sketch, "E338", {});
            skCircle(sketch, "E339", {"center": v(1439.75, -918.75) * mm, "radius": 4 * mm});
            skEllipticalArc(sketch, "E340", {});
            skLineSegment(sketch, "E341", {"start": v(1435.25, -911.54) * mm, "end": v(1435.25, -548.46) * mm});
            skEllipticalArc(sketch, "E342", {});
            skCircle(sketch, "E343", {"center": v(1439.75, -2031.25) * mm, "radius": 4 * mm});
            skLineSegment(sketch, "E344", {"start": v(621.1, -2066.75) * mm, "end": v(619.6, -2066.75) * mm});
            skLineSegment(sketch, "E345", {"start": v(619.6, -2076.75) * mm, "end": v(619.6, -2066.75) * mm});
            skLineSegment(sketch, "E346", {"start": v(621.1, -2076.75) * mm, "end": v(619.6, -2076.75) * mm});
            skLineSegment(sketch, "E347", {"start": v(621.1, -2066.75) * mm, "end": v(621.1, -2076.75) * mm});
            skLineSegment(sketch, "E348", {"start": v(167.32, -2022.75) * mm, "end": v(170.32, -2022.75) * mm});
            skLineSegment(sketch, "E349", {"start": v(167.32, -2029.75) * mm, "end": v(170.32, -2029.75) * mm});
            skLineSegment(sketch, "E350", {"start": v(170.32, -927.25) * mm, "end": v(170.32, -532.75) * mm});
            skLineSegment(sketch, "E351", {"start": v(167.32, -532.75) * mm, "end": v(167.32, -927.25) * mm});
            skLineSegment(sketch, "E352", {"start": v(167.32, -927.25) * mm, "end": v(170.32, -927.25) * mm});
            skLineSegment(sketch, "E353", {"start": v(167.32, -532.75) * mm, "end": v(170.32, -532.75) * mm});
            skLineSegment(sketch, "E354", {"start": v(167.32, -539.75) * mm, "end": v(170.32, -539.75) * mm});
            skLineSegment(sketch, "E355", {"start": v(170.28, -78.54) * mm, "end": v(1070.36, -78.54) * mm});
            skLineSegment(sketch, "E356", {"start": v(1070.32, -3803.42) * mm, "end": v(1073.32, -3803.42) * mm});
            skLineSegment(sketch, "E357", {"start": v(1073.32, -3797.14) * mm, "end": v(1070.32, -3797.14) * mm});
            skLineSegment(sketch, "E358", {"start": v(1070.32, -3797.14) * mm, "end": v(1070.32, -3907.14) * mm});
            skLineSegment(sketch, "E359", {"start": v(1073.32, -3797.14) * mm, "end": v(1073.32, -3907.14) * mm});
            skLineSegment(sketch, "E360", {"start": v(1073.32, -3907.14) * mm, "end": v(1070.32, -3907.14) * mm});
            skLineSegment(sketch, "E361", {"start": v(170.28, -4548.43) * mm, "end": v(1070.36, -4548.43) * mm});
            skLineSegment(sketch, "E362", {"start": v(170.28, -4192.43) * mm, "end": v(1070.36, -4192.43) * mm});
            skLineSegment(sketch, "E363", {"start": v(1070.36, -4548.43) * mm, "end": v(1070.36, -4170.43) * mm});
            skLineSegment(sketch, "E364", {"start": v(1073.28, -4548.43) * mm, "end": v(1073.28, -4170.43) * mm});
            skLineSegment(sketch, "E365", {"start": v(1073.28, -4548.43) * mm, "end": v(1070.36, -4548.43) * mm});
            skLineSegment(sketch, "E366", {"start": v(1070.36, -4170.43) * mm, "end": v(1073.28, -4170.43) * mm});
            skLineSegment(sketch, "E367", {"start": v(1070.36, -4177.43) * mm, "end": v(1073.28, -4177.43) * mm});
            skLineSegment(sketch, "E368", {"start": v(170.28, -4177.43) * mm, "end": v(167.36, -4177.43) * mm});
            skLineSegment(sketch, "E369", {"start": v(170.28, -4170.43) * mm, "end": v(167.36, -4170.43) * mm});
            skLineSegment(sketch, "E370", {"start": v(167.36, -4548.43) * mm, "end": v(170.28, -4548.43) * mm});
            skLineSegment(sketch, "E371", {"start": v(167.36, -4548.43) * mm, "end": v(167.36, -4170.43) * mm});
            skLineSegment(sketch, "E372", {"start": v(170.28, -4548.43) * mm, "end": v(170.28, -4170.43) * mm});
            skLineSegment(sketch, "E373", {"start": v(167.36, -3058.54) * mm, "end": v(170.28, -3058.54) * mm});
            skLineSegment(sketch, "E374", {"start": v(2055.16, -4837.25) * mm, "end": v(3055.16, -4837.25) * mm});
            skLineSegment(sketch, "E375", {"start": v(1809.23, -3797.14) * mm, "end": v(1809.23, -3906.51) * mm});
            skLineSegment(sketch, "E376", {"start": v(2055.16, -5837.25) * mm, "end": v(2055.16, -4837.25) * mm});
            skLineSegment(sketch, "E377", {"start": v(3055.16, -5837.25) * mm, "end": v(2055.16, -5837.25) * mm});
            skLineSegment(sketch, "E378", {"start": v(3055.16, -4837.25) * mm, "end": v(3055.16, -5837.25) * mm});
            skLineSegment(sketch, "E379", {"start": v(-1274.6, -2680.54) * mm, "end": v(-1271.68, -2680.54) * mm});
            skLineSegment(sketch, "E380", {"start": v(-1274.6, -2687.54) * mm, "end": v(-1271.68, -2687.54) * mm});
            skLineSegment(sketch, "E381", {"start": v(1435.23, -3812.49) * mm, "end": v(1435.23, -3890.8) * mm});
            skLineSegment(sketch, "E382", {"start": v(1444.2, -3906.51) * mm, "end": v(1439.53, -3906.51) * mm});
            skArc(sketch, "E383", {"start": v(1435.23, -3890.8) * mm, "mid": v(1431.38, -3900.3) * mm, "end": v(1439.53, -3906.51) * mm});
            skArc(sketch, "E384", {"start": v(1439.73, -3796.78) * mm, "mid": v(1431.56, -3802.94) * mm, "end": v(1435.23, -3812.49) * mm});
            skCircle(sketch, "E385", {"center": v(1439.73, -3898.01) * mm, "radius": 4 * mm});
            skCircle(sketch, "E386", {"center": v(1439.73, -3805.28) * mm, "radius": 4 * mm});
            skLineSegment(sketch, "E387", {"start": v(170.32, -3907.14) * mm, "end": v(170.32, -3797.14) * mm});
            skLineSegment(sketch, "E388", {"start": v(167.32, -3907.14) * mm, "end": v(170.32, -3907.14) * mm});
            skLineSegment(sketch, "E389", {"start": v(167.32, -3797.14) * mm, "end": v(170.32, -3797.14) * mm});
            skLineSegment(sketch, "E390", {"start": v(167.32, -3797.14) * mm, "end": v(167.32, -3907.14) * mm});
            skLineSegment(sketch, "E391", {"start": v(167.32, -3900.14) * mm, "end": v(170.32, -3900.14) * mm});
            skLineSegment(sketch, "E392", {"start": v(170.28, -3058.54) * mm, "end": v(1070.36, -3058.54) * mm});
            skLineSegment(sketch, "E393", {"start": v(1073.28, -3058.54) * mm, "end": v(1070.36, -3058.54) * mm});
            skLineSegment(sketch, "E394", {"start": v(170.32, -3818.14) * mm, "end": v(1070.32, -3818.14) * mm});
            skLineSegment(sketch, "E395", {"start": v(1070.32, -3816.14) * mm, "end": v(170.32, -3816.14) * mm});
            skLineSegment(sketch, "E396", {"start": v(170.32, -3797.14) * mm, "end": v(1070.32, -3797.14) * mm});
            skLineSegment(sketch, "E397", {"start": v(170.32, -3907.14) * mm, "end": v(1070.32, -3907.14) * mm});
            skCircle(sketch, "E398", {"center": v(-660.25, -541.25) * mm, "radius": 4 * mm});
            skEllipticalArc(sketch, "E399", {});
            skLineSegment(sketch, "E400", {"start": v(-660.25, -532.75) * mm, "end": v(-290.75, -532.75) * mm});
            skCircle(sketch, "E401", {"center": v(-660.25, -918.75) * mm, "radius": 4 * mm});
            skEllipticalArc(sketch, "E402", {});
            skLineSegment(sketch, "E403", {"start": v(-1271.64, -2022.75) * mm, "end": v(-1274.64, -2022.75) * mm});
            skLineSegment(sketch, "E404", {"start": v(-1271.64, -532.75) * mm, "end": v(-1271.64, -927.25) * mm});
            skLineSegment(sketch, "E405", {"start": v(-1274.64, -927.25) * mm, "end": v(-1274.64, -532.75) * mm});
            skLineSegment(sketch, "E406", {"start": v(-1271.64, -927.25) * mm, "end": v(-1274.64, -927.25) * mm});
            skLineSegment(sketch, "E407", {"start": v(-1271.64, -532.75) * mm, "end": v(-1274.64, -532.75) * mm});
            skLineSegment(sketch, "E408", {"start": v(-1271.68, -78.54) * mm, "end": v(-1274.6, -78.54) * mm});
            skLineSegment(sketch, "E409", {"start": v(-1274.6, -1190.54) * mm, "end": v(-1271.68, -1190.54) * mm});
            skLineSegment(sketch, "E410", {"start": v(-1271.68, -1568.54) * mm, "end": v(-1274.6, -1568.54) * mm});
            skLineSegment(sketch, "E411", {"start": v(-1274.6, -1568.54) * mm, "end": v(-1274.6, -1190.54) * mm});
            skLineSegment(sketch, "E412", {"start": v(-1271.68, -1568.54) * mm, "end": v(-1271.68, -1190.54) * mm});
            skLineSegment(sketch, "E413", {"start": v(-1274.6, -1197.54) * mm, "end": v(-1271.68, -1197.54) * mm});
            skCircle(sketch, "E414", {"center": v(-660.25, -2408.75) * mm, "radius": 4 * mm});
            skEllipticalArc(sketch, "E415", {});
            skLineSegment(sketch, "E416", {"start": v(-660.61, -2417.25) * mm, "end": v(-290.75, -2417.25) * mm});
            skLineSegment(sketch, "E417", {"start": v(-664.75, -2401.54) * mm, "end": v(-664.75, -2038.46) * mm});
            skLineSegment(sketch, "E418", {"start": v(-290.75, -2022.75) * mm, "end": v(-290.75, -2417.25) * mm});
            skLineSegment(sketch, "E419", {"start": v(-1271.64, -2417.25) * mm, "end": v(-1274.64, -2417.25) * mm});
            skLineSegment(sketch, "E420", {"start": v(-1271.64, -2022.75) * mm, "end": v(-1271.64, -2417.25) * mm});
            skLineSegment(sketch, "E421", {"start": v(-1274.64, -2417.25) * mm, "end": v(-1274.64, -2022.75) * mm});
            skLineSegment(sketch, "E422", {"start": v(-1932.6, -1568.54) * mm, "end": v(-1932.6, -1190.54) * mm});
            skLineSegment(sketch, "E423", {"start": v(-1929.68, -1190.54) * mm, "end": v(-1932.6, -1190.54) * mm});
            skLineSegment(sketch, "E424", {"start": v(-1929.68, -1197.54) * mm, "end": v(-1932.6, -1197.54) * mm});
            skLineSegment(sketch, "E425", {"start": v(-1932.6, -78.54) * mm, "end": v(-1929.68, -78.54) * mm});
            skCircle(sketch, "E426", {"center": v(-1602.14, -2071.75) * mm, "radius": 13 * mm});
            skCircle(sketch, "E427", {"center": v(-1602.14, -2071.75) * mm, "radius": 14 * mm});
            skLineSegment(sketch, "E428", {"start": v(-1602.9, -2076.75) * mm, "end": v(-1602.9, -2066.75) * mm});
            skLineSegment(sketch, "E429", {"start": v(-1601.4, -2066.75) * mm, "end": v(-1602.9, -2066.75) * mm});
            skLineSegment(sketch, "E430", {"start": v(-1601.4, -2066.75) * mm, "end": v(-1601.4, -2076.75) * mm});
            skLineSegment(sketch, "E431", {"start": v(-1601.4, -2076.75) * mm, "end": v(-1602.9, -2076.75) * mm});
            skLineSegment(sketch, "E432", {"start": v(-1932.64, -2417.25) * mm, "end": v(-1929.64, -2417.25) * mm});
            skLineSegment(sketch, "E433", {"start": v(-1932.64, -2022.75) * mm, "end": v(-1932.64, -2417.25) * mm});
            skLineSegment(sketch, "E434", {"start": v(-1929.64, -2417.25) * mm, "end": v(-1929.64, -2022.75) * mm});
            skLineSegment(sketch, "E435", {"start": v(-1929.68, -2680.54) * mm, "end": v(-1932.6, -2680.54) * mm});
            skLineSegment(sketch, "E436", {"start": v(-1929.68, -2687.54) * mm, "end": v(-1932.6, -2687.54) * mm});
            skLineSegment(sketch, "E437", {"start": v(-1271.64, -539.75) * mm, "end": v(-1274.64, -539.75) * mm});
            skLineSegment(sketch, "E438", {"start": v(-1271.64, -2029.75) * mm, "end": v(-1274.64, -2029.75) * mm});
            skLineSegment(sketch, "E439", {"start": v(-660.61, -927.25) * mm, "end": v(-290.75, -927.25) * mm});
            skLineSegment(sketch, "E440", {"start": v(-664.75, -911.54) * mm, "end": v(-664.75, -548.46) * mm});
            skLineSegment(sketch, "E441", {"start": v(-290.75, -532.75) * mm, "end": v(-290.75, -927.25) * mm});
            skCircle(sketch, "E442", {"center": v(-660.25, -2031.25) * mm, "radius": 4 * mm});
            skEllipticalArc(sketch, "E443", {});
            skLineSegment(sketch, "E444", {"start": v(-660.25, -2022.75) * mm, "end": v(-290.75, -2022.75) * mm});
            skLineSegment(sketch, "E445", {"start": v(-1274.6, -4548.07) * mm, "end": v(-1274.6, -4170.07) * mm});
            skLineSegment(sketch, "E446", {"start": v(-1271.68, -4548.07) * mm, "end": v(-1271.68, -4170.07) * mm});
            skLineSegment(sketch, "E447", {"start": v(-1271.68, -4548.07) * mm, "end": v(-1274.6, -4548.07) * mm});
            skLineSegment(sketch, "E448", {"start": v(-1274.64, -3796.78) * mm, "end": v(-1274.64, -3906.78) * mm});
            skLineSegment(sketch, "E449", {"start": v(-1274.6, -4170.07) * mm, "end": v(-1271.68, -4170.07) * mm});
            skLineSegment(sketch, "E450", {"start": v(-1271.64, -3906.78) * mm, "end": v(-1274.64, -3906.78) * mm});
            skLineSegment(sketch, "E451", {"start": v(-1271.64, -3796.78) * mm, "end": v(-1271.64, -3906.78) * mm});
            skLineSegment(sketch, "E452", {"start": v(-1271.64, -3796.78) * mm, "end": v(-1274.64, -3796.78) * mm});
            skLineSegment(sketch, "E453", {"start": v(-1274.64, -3803.78) * mm, "end": v(-1271.64, -3803.78) * mm});
            skLineSegment(sketch, "E454", {"start": v(-1271.68, -3058.54) * mm, "end": v(-1274.6, -3058.54) * mm});
            skLineSegment(sketch, "E455", {"start": v(-1932.64, -539.75) * mm, "end": v(-1929.64, -539.75) * mm});
            skLineSegment(sketch, "E456", {"start": v(-1932.64, -2029.75) * mm, "end": v(-1929.64, -2029.75) * mm});
            skLineSegment(sketch, "E457", {"start": v(-1932.64, -532.75) * mm, "end": v(-1929.64, -532.75) * mm});
            skLineSegment(sketch, "E458", {"start": v(-1932.64, -927.25) * mm, "end": v(-1929.64, -927.25) * mm});
            skLineSegment(sketch, "E459", {"start": v(-1932.64, -532.75) * mm, "end": v(-1932.64, -927.25) * mm});
            skLineSegment(sketch, "E460", {"start": v(-1929.64, -927.25) * mm, "end": v(-1929.64, -532.75) * mm});
            skLineSegment(sketch, "E461", {"start": v(-1929.64, -908.25) * mm, "end": v(-1929.64, -878.25) * mm});
            skLineSegment(sketch, "E462", {"start": v(-1932.64, -2022.75) * mm, "end": v(-1929.64, -2022.75) * mm});
            skLineSegment(sketch, "E463", {"start": v(-1932.6, -1568.54) * mm, "end": v(-1929.68, -1568.54) * mm});
            skLineSegment(sketch, "E464", {"start": v(-1929.68, -1568.54) * mm, "end": v(-1929.68, -1190.54) * mm});
            skLineSegment(sketch, "E465", {"start": v(-1929.64, -3906.78) * mm, "end": v(-1929.64, -3796.78) * mm});
            skLineSegment(sketch, "E466", {"start": v(-1932.64, -3906.78) * mm, "end": v(-1929.64, -3906.78) * mm});
            skLineSegment(sketch, "E467", {"start": v(-1932.64, -3796.78) * mm, "end": v(-1929.64, -3796.78) * mm});
            skLineSegment(sketch, "E468", {"start": v(-1932.64, -3796.78) * mm, "end": v(-1932.64, -3906.78) * mm});
            skLineSegment(sketch, "E469", {"start": v(-1932.64, -3803.78) * mm, "end": v(-1929.64, -3803.78) * mm});
            skLineSegment(sketch, "E470", {"start": v(-1929.68, -4170.07) * mm, "end": v(-1932.6, -4170.07) * mm});
            skLineSegment(sketch, "E471", {"start": v(-1932.6, -4548.07) * mm, "end": v(-1932.6, -4170.07) * mm});
            skLineSegment(sketch, "E472", {"start": v(-1929.68, -4548.07) * mm, "end": v(-1929.68, -4170.07) * mm});
            skLineSegment(sketch, "E473", {"start": v(-1932.6, -4548.07) * mm, "end": v(-1929.68, -4548.07) * mm});
            skLineSegment(sketch, "E474", {"start": v(-1929.68, -4177.07) * mm, "end": v(-1932.6, -4177.07) * mm});
            skLineSegment(sketch, "E475", {"start": v(-1932.6, -3058.54) * mm, "end": v(-1929.68, -3058.54) * mm});
            skLineSegment(sketch, "E476", {"start": v(-1274.6, -4177.07) * mm, "end": v(-1271.68, -4177.07) * mm});
            skCircle(sketch, "E477", {"center": v(-660.25, -3898.01) * mm, "radius": 4 * mm});
            skCircle(sketch, "E478", {"center": v(-660.25, -3805.28) * mm, "radius": 4 * mm});
            skLineSegment(sketch, "E479", {"start": v(-655.79, -3906.51) * mm, "end": v(-290.75, -3906.51) * mm});
            skLineSegment(sketch, "E480", {"start": v(-660.62, -3796.78) * mm, "end": v(-290.75, -3797.14) * mm});
            skLineSegment(sketch, "E481", {"start": v(-290.75, -3797.14) * mm, "end": v(-290.75, -3906.51) * mm});
            skLineSegment(sketch, "E482", {"start": v(-664.75, -3812.49) * mm, "end": v(-664.75, -3890.8) * mm});
            skLineSegment(sketch, "E483", {"start": v(-655.79, -3906.51) * mm, "end": v(-660.46, -3906.51) * mm});
            skArc(sketch, "E484", {"start": v(-664.75, -3890.8) * mm, "mid": v(-668.6, -3900.3) * mm, "end": v(-660.46, -3906.51) * mm});
            skArc(sketch, "E485", {"start": v(-660.25, -3796.78) * mm, "mid": v(-668.43, -3802.94) * mm, "end": v(-664.75, -3812.49) * mm});
            skLineSegment(sketch, "E486", {"start": v(-1929.64, 5032.75) * mm, "end": v(-1274.64, 5032.75) * mm});
            skLineSegment(sketch, "E487", {"start": v(-1929.64, 5427.25) * mm, "end": v(-1274.64, 5427.25) * mm});
            skLineSegment(sketch, "E488", {"start": v(-1929.64, 5408.25) * mm, "end": v(-1274.64, 5408.25) * mm});
            skLineSegment(sketch, "E489", {"start": v(-1929.64, 3542.75) * mm, "end": v(-1274.64, 3542.75) * mm});
            skLineSegment(sketch, "E490", {"start": v(-1929.64, 3937.25) * mm, "end": v(-1274.64, 3937.25) * mm});
            skLineSegment(sketch, "E491", {"start": v(-1929.64, 3918.25) * mm, "end": v(-1274.64, 3918.25) * mm});
            skLineSegment(sketch, "E492", {"start": v(-1929.68, 3257.46) * mm, "end": v(-1274.6, 3257.46) * mm});
            skLineSegment(sketch, "E493", {"start": v(-1929.68, 4391.46) * mm, "end": v(-1274.6, 4391.46) * mm});
            skLineSegment(sketch, "E494", {"start": v(-1929.68, 4747.46) * mm, "end": v(-1274.6, 4747.46) * mm});
            skArc(sketch, "E495", {"start": v(-1530.41, 5408.25) * mm, "mid": v(-1532.36, 5407.44) * mm, "end": v(-1533.16, 5405.5) * mm});
            skLineSegment(sketch, "E496", {"start": v(-1533.16, 5405.5) * mm, "end": v(-1533.16, 5391.25) * mm});
            skLineSegment(sketch, "E497", {"start": v(-1662.16, 5382.25) * mm, "end": v(-1542.16, 5382.25) * mm});
            skArc(sketch, "E498", {"start": v(-1542.16, 5382.25) * mm, "mid": v(-1535.8, 5384.88) * mm, "end": v(-1533.16, 5391.25) * mm});
            skLineSegment(sketch, "E499", {"start": v(1439.75, 957.25) * mm, "end": v(1809.25, 957.25) * mm});
            skLineSegment(sketch, "E500", {"start": v(1439.39, 562.75) * mm, "end": v(1809.25, 562.75) * mm});
            skLineSegment(sketch, "E501", {"start": v(1439.75, 2447.25) * mm, "end": v(1809.25, 2447.25) * mm});
            skLineSegment(sketch, "E502", {"start": v(1439.39, 2052.75) * mm, "end": v(1809.25, 2052.75) * mm});
            skLineSegment(sketch, "E503", {"start": v(1439.75, 5427.25) * mm, "end": v(1809.25, 5427.25) * mm});
            skLineSegment(sketch, "E504", {"start": v(1439.39, 5032.75) * mm, "end": v(1809.25, 5032.75) * mm});
            skLineSegment(sketch, "E505", {"start": v(1439.75, 3937.25) * mm, "end": v(1809.25, 3937.25) * mm});
            skLineSegment(sketch, "E506", {"start": v(1439.39, 3542.75) * mm, "end": v(1809.25, 3542.75) * mm});
            skLineSegment(sketch, "E507", {"start": v(-1929.68, 1767.46) * mm, "end": v(-1274.6, 1767.46) * mm});
            skLineSegment(sketch, "E508", {"start": v(-1929.68, 1411.46) * mm, "end": v(-1274.6, 1411.46) * mm});
            skArc(sketch, "E509", {"start": v(-1530.41, 2428.25) * mm, "mid": v(-1532.36, 2427.44) * mm, "end": v(-1533.16, 2425.5) * mm});
            skLineSegment(sketch, "E510", {"start": v(-1662.16, 2402.25) * mm, "end": v(-1542.16, 2402.25) * mm});
            skArc(sketch, "E511", {"start": v(-1542.16, 2402.25) * mm, "mid": v(-1535.8, 2404.88) * mm, "end": v(-1533.16, 2411.25) * mm});
            skLineSegment(sketch, "E512", {"start": v(-1662.16, 2224) * mm, "end": v(-1542.16, 2224) * mm});
            skArc(sketch, "E513", {"start": v(-1530.41, 2250) * mm, "mid": v(-1532.36, 2249.2) * mm, "end": v(-1533.16, 2247.25) * mm});
            skArc(sketch, "E514", {"start": v(-1530.41, 700.58) * mm, "mid": v(-1532.36, 699.77) * mm, "end": v(-1533.16, 697.83) * mm});
            skLineSegment(sketch, "E515", {"start": v(-1662.16, 674.58) * mm, "end": v(-1542.16, 674.58) * mm});
            skArc(sketch, "E516", {"start": v(-1542.16, 674.58) * mm, "mid": v(-1535.8, 677.21) * mm, "end": v(-1533.16, 683.58) * mm});
            skArc(sketch, "E517", {"start": v(-1542.16, 793.4) * mm, "mid": v(-1535.8, 796.04) * mm, "end": v(-1533.16, 802.4) * mm});
            skLineSegment(sketch, "E518", {"start": v(-1662.16, 793.4) * mm, "end": v(-1542.16, 793.4) * mm});
            skLineSegment(sketch, "E519", {"start": v(-1533.16, 2425.5) * mm, "end": v(-1533.16, 2411.25) * mm});
            skLineSegment(sketch, "E520", {"start": v(-1533.16, 2247.25) * mm, "end": v(-1533.16, 2233) * mm});
            skArc(sketch, "E521", {"start": v(-1542.16, 2224) * mm, "mid": v(-1535.8, 2226.63) * mm, "end": v(-1533.16, 2233) * mm});
            skLineSegment(sketch, "E522", {"start": v(-1533.16, 816.66) * mm, "end": v(-1533.16, 802.4) * mm});
            skLineSegment(sketch, "E523", {"start": v(-1533.16, 935.5) * mm, "end": v(-1533.16, 921.25) * mm});
            skArc(sketch, "E524", {"start": v(-1530.41, 938.25) * mm, "mid": v(-1532.36, 937.44) * mm, "end": v(-1533.16, 935.5) * mm});
            skLineSegment(sketch, "E525", {"start": v(-1662.16, 912.25) * mm, "end": v(-1542.16, 912.25) * mm});
            skArc(sketch, "E526", {"start": v(-1542.16, 912.25) * mm, "mid": v(-1535.8, 914.88) * mm, "end": v(-1533.16, 921.25) * mm});
            skArc(sketch, "E527", {"start": v(-1530.41, 819.4) * mm, "mid": v(-1532.36, 818.6) * mm, "end": v(-1533.16, 816.66) * mm});
            skLineSegment(sketch, "E528", {"start": v(-1533.16, 697.83) * mm, "end": v(-1533.16, 683.58) * mm});
            skLineSegment(sketch, "E529", {"start": v(-1274.64, 3561.75) * mm, "end": v(-1929.64, 3561.75) * mm});
            skLineSegment(sketch, "E530", {"start": v(-1274.64, 5051.75) * mm, "end": v(-1929.64, 5051.75) * mm});
            skLineSegment(sketch, "E531", {"start": v(-1274.64, -2398.25) * mm, "end": v(-1929.64, -2398.25) * mm});
            skLineSegment(sketch, "E532", {"start": v(-1929.64, -2417.25) * mm, "end": v(-1274.64, -2417.25) * mm});
            skLineSegment(sketch, "E533", {"start": v(-1929.64, -2022.75) * mm, "end": v(-1274.64, -2022.75) * mm});
            skLineSegment(sketch, "E534", {"start": v(-1929.68, -2702.54) * mm, "end": v(-1274.6, -2702.54) * mm});
            skLineSegment(sketch, "E535", {"start": v(-1929.68, -1212.54) * mm, "end": v(-1274.6, -1212.54) * mm});
            skLineSegment(sketch, "E536", {"start": v(-1929.68, -1568.54) * mm, "end": v(-1274.6, -1568.54) * mm});
            skLineSegment(sketch, "E537", {"start": v(-1929.68, -78.54) * mm, "end": v(-1274.6, -78.54) * mm});
            skLineSegment(sketch, "E538", {"start": v(1444.2, -3906.51) * mm, "end": v(1809.23, -3906.51) * mm});
            skLineSegment(sketch, "E539", {"start": v(1439.37, -3796.78) * mm, "end": v(1809.23, -3797.14) * mm});
            skLineSegment(sketch, "E540", {"start": v(1439.75, -532.75) * mm, "end": v(1809.25, -532.75) * mm});
            skLineSegment(sketch, "E541", {"start": v(1439.39, -927.25) * mm, "end": v(1809.25, -927.25) * mm});
            skLineSegment(sketch, "E542", {"start": v(1439.75, -2022.75) * mm, "end": v(1809.25, -2022.75) * mm});
            skLineSegment(sketch, "E543", {"start": v(1439.39, -2417.25) * mm, "end": v(1809.25, -2417.25) * mm});
            skLineSegment(sketch, "E544", {"start": v(-1929.64, 700.58) * mm, "end": v(-1274.64, 700.58) * mm});
            skLineSegment(sketch, "E545", {"start": v(-1929.64, 2428.25) * mm, "end": v(-1274.64, 2428.25) * mm});
            skLineSegment(sketch, "E546", {"start": v(-1274.64, 2071.75) * mm, "end": v(-1929.64, 2071.75) * mm});
            skLineSegment(sketch, "E547", {"start": v(-1929.64, 2052.75) * mm, "end": v(-1274.64, 2052.75) * mm});
            skLineSegment(sketch, "E548", {"start": v(-1929.64, 2447.25) * mm, "end": v(-1274.64, 2447.25) * mm});
            skLineSegment(sketch, "E549", {"start": v(-1929.64, 938.25) * mm, "end": v(-1274.64, 938.25) * mm});
            skLineSegment(sketch, "E550", {"start": v(-1274.64, 581.75) * mm, "end": v(-1929.64, 581.75) * mm});
            skLineSegment(sketch, "E551", {"start": v(-1929.64, 562.75) * mm, "end": v(-1274.64, 562.75) * mm});
            skLineSegment(sketch, "E552", {"start": v(-1929.64, 957.25) * mm, "end": v(-1274.64, 957.25) * mm});
            skLineSegment(sketch, "E553", {"start": v(-1929.64, 2250) * mm, "end": v(-1274.64, 2250) * mm});
            skLineSegment(sketch, "E554", {"start": v(-1929.64, 819.4) * mm, "end": v(-1274.64, 819.4) * mm});
            skLineSegment(sketch, "E555", {"start": v(-1929.68, 277.46) * mm, "end": v(-1274.6, 277.46) * mm});
            skLineSegment(sketch, "E556", {"start": v(-1271.68, 2901.46) * mm, "end": v(-1274.6, 2901.46) * mm});
            skLineSegment(sketch, "E557", {"start": v(-1929.68, 2901.46) * mm, "end": v(-1929.68, 3279.46) * mm});
            skLineSegment(sketch, "E558", {"start": v(-1932.6, 2901.46) * mm, "end": v(-1932.6, 3279.46) * mm});
            skLineSegment(sketch, "E559", {"start": v(-1932.6, 2901.46) * mm, "end": v(-1929.68, 2901.46) * mm});
            skLineSegment(sketch, "E560", {"start": v(-1929.68, 2901.46) * mm, "end": v(-1274.6, 2901.46) * mm});
            skLineSegment(sketch, "E561", {"start": v(1073.28, 2901.46) * mm, "end": v(1073.28, 3279.46) * mm});
            skLineSegment(sketch, "E562", {"start": v(1070.36, 2901.46) * mm, "end": v(1070.36, 3279.46) * mm});
            skLineSegment(sketch, "E563", {"start": v(167.36, 2901.46) * mm, "end": v(167.36, 3279.46) * mm});
            skLineSegment(sketch, "E564", {"start": v(170.28, 2901.46) * mm, "end": v(170.28, 3279.46) * mm});
            skLineSegment(sketch, "E565", {"start": v(167.36, 2901.46) * mm, "end": v(170.28, 2901.46) * mm});
            skLineSegment(sketch, "E566", {"start": v(1073.28, 2901.46) * mm, "end": v(1070.36, 2901.46) * mm});
            skLineSegment(sketch, "E567", {"start": v(170.28, 2901.46) * mm, "end": v(1070.36, 2901.46) * mm});
            skLineSegment(sketch, "E568", {"start": v(-1274.64, -3815.78) * mm, "end": v(-1929.64, -3815.78) * mm});
            skLineSegment(sketch, "E569", {"start": v(-1929.64, -3796.78) * mm, "end": v(-1274.64, -3796.78) * mm});
            skLineSegment(sketch, "E570", {"start": v(-1929.64, -3906.78) * mm, "end": v(-1274.64, -3906.78) * mm});
            skLineSegment(sketch, "E571", {"start": v(-1929.64, -3817.78) * mm, "end": v(-1274.64, -3817.78) * mm});
            skLineSegment(sketch, "E572", {"start": v(-1929.68, -4192.07) * mm, "end": v(-1274.6, -4192.07) * mm});
            skLineSegment(sketch, "E573", {"start": v(-1929.68, -4548.07) * mm, "end": v(-1274.6, -4548.07) * mm});
            skLineSegment(sketch, "E574", {"start": v(-1929.68, -3058.54) * mm, "end": v(-1274.6, -3058.54) * mm});
            skLineSegment(sketch, "E575", {"start": v(-1929.64, -878.25) * mm, "end": v(-1274.64, -878.25) * mm});
            skLineSegment(sketch, "E576", {"start": v(-1274.64, -908.25) * mm, "end": v(-1929.64, -908.25) * mm});
            skLineSegment(sketch, "E577", {"start": v(-1929.64, -927.25) * mm, "end": v(-1274.64, -927.25) * mm});
            skLineSegment(sketch, "E578", {"start": v(-1929.64, -532.75) * mm, "end": v(-1274.64, -532.75) * mm});
            skLineSegment(sketch, "E579", {"start": v(-1929.64, -551.75) * mm, "end": v(-1274.64, -551.75) * mm});
            skLineSegment(sketch, "E580", {"start": v(-1929.64, -2041.75) * mm, "end": v(-1274.64, -2041.75) * mm});
            skLineSegment(sketch, "E581", {"start": v(1073.28, -78.54) * mm, "end": v(1073.28, 299.46) * mm});
            skLineSegment(sketch, "E582", {"start": v(1070.36, -78.54) * mm, "end": v(1070.36, 299.46) * mm});
            skLineSegment(sketch, "E583", {"start": v(-1274.6, -78.54) * mm, "end": v(-1274.6, 299.46) * mm});
            skLineSegment(sketch, "E584", {"start": v(-1271.68, -78.54) * mm, "end": v(-1271.68, 299.46) * mm});
            skLineSegment(sketch, "E585", {"start": v(167.36, -78.54) * mm, "end": v(167.36, 299.46) * mm});
            skLineSegment(sketch, "E586", {"start": v(170.28, -78.54) * mm, "end": v(170.28, 299.46) * mm});
            skLineSegment(sketch, "E587", {"start": v(-1929.68, -78.54) * mm, "end": v(-1929.68, 299.46) * mm});
            skLineSegment(sketch, "E588", {"start": v(-1932.6, -78.54) * mm, "end": v(-1932.6, 299.46) * mm});
            skLineSegment(sketch, "E589", {"start": v(-44.84, 5592.75) * mm, "end": v(-44.84, -4837.25) * mm});
            skLineSegment(sketch, "E590", {"start": v(2055.16, -3347.25) * mm, "end": v(-2144.84, -3347.25) * mm});
            skLineSegment(sketch, "E591", {"start": v(2055.16, -1857.25) * mm, "end": v(-2144.84, -1857.25) * mm});
            skLineSegment(sketch, "E592", {"start": v(2055.16, -367.25) * mm, "end": v(-2144.84, -367.25) * mm});
            skLineSegment(sketch, "E593", {"start": v(2055.16, 4102.75) * mm, "end": v(-2144.84, 4102.75) * mm});
            skLineSegment(sketch, "E594", {"start": v(2055.16, 2612.75) * mm, "end": v(-2144.84, 2612.75) * mm});
            skLineSegment(sketch, "E595", {"start": v(2055.16, 1122.75) * mm, "end": v(-2144.84, 1122.75) * mm});
            skLineSegment(sketch, "E596", {"start": v(-1274.6, -3058.54) * mm, "end": v(-1274.6, -2680.54) * mm});
            skLineSegment(sketch, "E597", {"start": v(-1271.68, -3058.54) * mm, "end": v(-1271.68, -2680.54) * mm});
            skLineSegment(sketch, "E598", {"start": v(-1929.68, -3058.54) * mm, "end": v(-1929.68, -2680.54) * mm});
            skLineSegment(sketch, "E599", {"start": v(-1932.6, -3058.54) * mm, "end": v(-1932.6, -2680.54) * mm});
            skLineSegment(sketch, "E600", {"start": v(1073.28, -3058.54) * mm, "end": v(1073.28, -2680.54) * mm});
            skLineSegment(sketch, "E601", {"start": v(1070.36, -3058.54) * mm, "end": v(1070.36, -2680.54) * mm});
            skLineSegment(sketch, "E602", {"start": v(167.36, -3058.54) * mm, "end": v(167.36, -2680.54) * mm});
            skLineSegment(sketch, "E603", {"start": v(170.28, -3058.54) * mm, "end": v(170.28, -2680.54) * mm});
            skLineSegment(sketch, "E604", {"start": v(-1271.68, 2901.46) * mm, "end": v(-1271.68, 3279.46) * mm});
            skLineSegment(sketch, "E605", {"start": v(-1274.6, 2901.46) * mm, "end": v(-1274.6, 3279.46) * mm});
            const initialGuessF0  = {"E42": [1.4397505876, 5.0412485154, 0, -0.334646, 0.0085000084, 0.0085000084, 0, 2.583686], "E44": [1.4397505876, 3.9287485306000005, 0, 0.334646, 0.0085000084, 0.0085000084, 0, 2.583686], "E46": [1.4397505876, 3.5512485236, 0, -0.334646, 0.0085000084, 0.0085000084, 0, 2.583686], "E71": [1.4397505876, 5.4187485224000005, 0, 0.334646, 0.0085000084, 0.0085000084, 0, 2.583686], "E132": [1.4397505876, 0.5712485145999997, 0, -0.334646, 0.0085000084, 0.0085000084, 0, 2.583686], "E169": [1.4397505876, 2.4387485133999998, 0, 0.334646, 0.0085000084, 0.0085000084, 0, 2.583686], "E171": [1.4397505876, 2.0612485318, 0, -0.334646, 0.0085000084, 0.0085000084, 0, 2.583686], "E174": [1.4397505876, 0.9487485216000002, 0, 0.334646, 0.0085000084, 0.0085000084, 0, 2.583686], "E180": [-0.6602494034, 5.4187485224000005, 0, 0.334646, 0.0085000084, 0.0085000084, 0, 2.583686], "E184": [-0.6602494034, 5.0412485154, 0, -0.334646, 0.0085000084, 0.0085000084, 0, 2.583686], "E187": [-0.6602494034, 3.9287485306000005, 0, 0.334646, 0.0085000084, 0.0085000084, 0, 2.583686], "E190": [-0.6602494034, 3.5512485236, 0, -0.334646, 0.0085000084, 0.0085000084, 0, 2.583686], "E225": [-0.6602494034, 2.4387485133999998, 0, 0.334646, 0.0085000084, 0.0085000084, 0, 2.583686], "E260": [-0.6602494034, 2.0612485318, 0, -0.334646, 0.0085000084, 0.0085000084, 0, 2.583686], "E264": [-0.6602494034, 0.9487485216000002, 0, 0.334646, 0.0085000084, 0.0085000084, 0, 2.583686], "E267": [-0.6602494034, 0.5712485145999997, 0, -0.334646, 0.0085000084, 0.0085000084, 0, 2.583686], "E293": [1.4397505876, -2.408751469, 0, -0.334646, 0.0085000084, 0.0085000084, 0, 2.583686], "E338": [1.4397505876, -0.5412514702, 0, 0.334646, 0.0085000084, 0.0085000084, 0, 2.583686], "E340": [1.4397505876, -0.9187514772000004, 0, -0.334646, 0.0085000084, 0.0085000084, 0, 2.583686], "E342": [1.4397505876, -2.031251487400001, 0, 0.334646, 0.0085000084, 0.0085000084, 0, 2.583686], "E399": [-0.6602494034, -0.5412514702, 0, 0.334646, 0.0085000084, 0.0085000084, 0, 2.583686], "E402": [-0.6602494034, -0.9187514772000004, 0, -0.334646, 0.0085000084, 0.0085000084, 0, 2.583686], "E415": [-0.6602494034, -2.408751469, 0, -0.334646, 0.0085000084, 0.0085000084, 0, 2.583686], "E443": [-0.6602494034, -2.031251487400001, 0, 0.334646, 0.0085000084, 0.0085000084, 0, 2.583686]};
            skSetInitialGuess(sketch, initialGuessF0);
            skSolve(sketch);
        }
        {
            var Q0;
            Q0=qCreatedBy(makeId("Right.planeOp"),FACE);
            var sketch = newSketch(context, id + "F1", { "sketchPlane" : qUnion([Q0])});
            skLineSegment(sketch, "E606", {"start": v(-8535, 2931.01) * mm, "end": v(-8165.5, 2931.01) * mm});
            skLineSegment(sketch, "E607", {"start": v(-8165.5, 2931.01) * mm, "end": v(-8165.5, 2536.52) * mm});
            skLineSegment(sketch, "E608", {"start": v(-8165.5, 2536.52) * mm, "end": v(-8535, 2536.52) * mm});
            skLineSegment(sketch, "E609", {"start": v(-8535, 2915.26) * mm, "end": v(-8535, 2552.27) * mm});
            skLineSegment(sketch, "E610", {"start": v(-8165.5, 2733.77) * mm, "end": v(-8535, 2733.77) * mm, "construction": true});
            skArc(sketch, "E611", {"start": v(-8535, 2552.27) * mm, "mid": v(-8542.86, 2544.4) * mm, "end": v(-8535, 2536.52) * mm});
            skArc(sketch, "E612", {"start": v(-8535, 2931.01) * mm, "mid": v(-8542.86, 2923.14) * mm, "end": v(-8535, 2915.26) * mm});
            skCircle(sketch, "E613", {"center": v(-8535, 2923.14) * mm, "radius": 4 * mm});
            skCircle(sketch, "E614", {"center": v(-8535, 2544.4) * mm, "radius": 4 * mm});
            skSolve(sketch);
        }
        {
            var Q0;
            Q0 = qSketchRegion(id + "F1", true);
            extrude(context, id + "F2", {"entities" : qUnion([Q0]), "depth" : 3.17 * mm});
        }
        {
            var Q0;
            Q0=makeQuery(id+"F2.opExtrude","CAP_FACE",FACE,{"disambiguationData":[OSD([sQuery(id+"F1.wireOp",EDGE,"E606"),sQuery(id+"F1.wireOp",EDGE,"E607"),sQuery(id+"F1.wireOp",EDGE,"E608"),sQuery(id+"F1.wireOp",EDGE,"E609"),sQuery(id+"F1.wireOp",EDGE,"E611"),sQuery(id+"F1.wireOp",EDGE,"E612"),sQuery(id+"F1.wireOp",EDGE,"E613"),sQuery(id+"F1.wireOp",EDGE,"E614")])],"isStart":true});
            var sketch = newSketch(context, id + "F3", { "sketchPlane" : qUnion([Q0])});
            skLineSegment(sketch, "E615.2", {"start": v(8165.5, 2931.01) * mm, "end": v(8165.5, 2536.52) * mm});
            skLineSegment(sketch, "E616", {"start": v(8165.5, 2931.01) * mm, "end": v(8527.45, 2931.01) * mm});
            skLineSegment(sketch, "E617", {"start": v(8527.45, 2931.01) * mm, "end": v(8527.45, 2536.52) * mm});
            skLineSegment(sketch, "E618", {"start": v(8527.45, 2536.52) * mm, "end": v(8165.5, 2536.52) * mm});
            skSolve(sketch);
        }
        {
            var Q0;
            Q0 = qSketchRegion(id + "F3", true);
            extrude(context, id + "F4", {"entities" : qUnion([Q0]), "depth" : 900.1 * mm});
        }
        {
            var Q0;
            Q0=makeQuery(id+"F2.opExtrude","CAP_FACE",FACE,{"disambiguationData":[OSD([sQuery(id+"F1.wireOp",EDGE,"E606"),sQuery(id+"F1.wireOp",EDGE,"E607"),sQuery(id+"F1.wireOp",EDGE,"E608"),sQuery(id+"F1.wireOp",EDGE,"E609"),sQuery(id+"F1.wireOp",EDGE,"E611"),sQuery(id+"F1.wireOp",EDGE,"E612"),sQuery(id+"F1.wireOp",EDGE,"E613"),sQuery(id+"F1.wireOp",EDGE,"E614")])],"isStart":true});
            var sketch = newSketch(context, id + "F5", { "sketchPlane" : qUnion([Q0])});
            skLineSegment(sketch, "E619.0", {"start": v(8165.5, 2931.01) * mm, "end": v(8165.5, 2536.52) * mm});
            skLineSegment(sketch, "E619.1", {"start": v(8165.5, 2931.01) * mm, "end": v(8527.45, 2931.01) * mm});
            skLineSegment(sketch, "E619.2", {"start": v(8527.45, 2931.01) * mm, "end": v(8527.45, 2536.52) * mm});
            skLineSegment(sketch, "E619.3", {"start": v(8527.45, 2536.52) * mm, "end": v(8165.5, 2536.52) * mm});
            skSolve(sketch);
        }
        {
            var Q0;
            Q0 = qSketchRegion(id + "F5", true);
            extrude(context, id + "F6", {"entities" : qUnion([Q0]), "depth" : 654.05 * mm});
        }
        {
            var Q0;
            Q0=makeQuery(id+"F6.opExtrude","SWEPT_BODY",BODY,{"disambiguationData":[OSD([sQuery(id+"F5.wireOp",EDGE,"E619.0"),sQuery(id+"F5.wireOp",EDGE,"E619.1"),sQuery(id+"F5.wireOp",EDGE,"E619.2"),sQuery(id+"F5.wireOp",EDGE,"E619.3")])]});
            transform(context, id + "F7", {"entities" : qUnion([Q0]), "transformType" : TransformType.TRANSLATION_3D, "dx" : -1275.5 * mm, "dy" : 0 * mm, "dz" : 3188.52 * mm, "makeCopy" : false});
        }
        {
            var Q0;
            Q0=makeQuery(id+"F4.opExtrude","SWEPT_BODY",BODY,{"disambiguationData":[OSD([sQuery(id+"F3.wireOp",EDGE,"E615.2"),sQuery(id+"F3.wireOp",EDGE,"E616"),sQuery(id+"F3.wireOp",EDGE,"E617"),sQuery(id+"F3.wireOp",EDGE,"E618")])]});
            transform(context, id + "F8", {"entities" : qUnion([Q0]), "transformType" : TransformType.TRANSLATION_3D, "dx" : 1070.48 * mm, "dy" : 0 * mm, "dz" : 3167.6 * mm, "makeCopy" : false});
        }
        {
            var Q0;
            Q0=makeQuery(id+"F4.opExtrude","SWEPT_BODY",BODY,{"disambiguationData":[OSD([sQuery(id+"F3.wireOp",EDGE,"E615.2"),sQuery(id+"F3.wireOp",EDGE,"E616"),sQuery(id+"F3.wireOp",EDGE,"E617"),sQuery(id+"F3.wireOp",EDGE,"E618")])]});
            transform(context, id + "F9", {"entities" : qUnion([Q0]), "transformType" : TransformType.TRANSLATION_3D, "dx" : 0 * mm, "dy" : 0 * mm, "dz" : -671.32 * mm, "makeCopy" : true});
        }
        {
            var Q0;
            Q0=makeQuery(id+"F9.opPattern","COPY",BODY,{"derivedFrom":makeQuery(id+"F4.opExtrude","SWEPT_BODY",BODY,{"disambiguationData":[OSD([sQuery(id+"F3.wireOp",EDGE,"E615.2"),sQuery(id+"F3.wireOp",EDGE,"E616"),sQuery(id+"F3.wireOp",EDGE,"E617"),sQuery(id+"F3.wireOp",EDGE,"E618")])]}),"instanceName":"1"});
            transform(context, id + "F10", {"entities" : qUnion([Q0]), "transformType" : TransformType.TRANSLATION_3D, "dx" : 0 * mm, "dy" : 0 * mm, "dz" : -1490.98 * mm, "makeCopy" : true});
        }
        {
            var Q0;
            Q0=makeQuery(id+"F10.opPattern","COPY",BODY,{"derivedFrom":makeQuery(id+"F9.opPattern","COPY",BODY,{"derivedFrom":makeQuery(id+"F4.opExtrude","SWEPT_BODY",BODY,{"disambiguationData":[OSD([sQuery(id+"F3.wireOp",EDGE,"E615.2"),sQuery(id+"F3.wireOp",EDGE,"E616"),sQuery(id+"F3.wireOp",EDGE,"E617"),sQuery(id+"F3.wireOp",EDGE,"E618")])]}),"instanceName":"1"}),"instanceName":"1"});
            transform(context, id + "F11", {"entities" : qUnion([Q0]), "transformType" : TransformType.TRANSLATION_3D, "dx" : 0 * mm, "dy" : 0 * mm, "dz" : -1490.98 * mm, "makeCopy" : true});
        }
        {
            var Q0;
            Q0=makeQuery(id+"F11.opPattern","COPY",BODY,{"derivedFrom":makeQuery(id+"F10.opPattern","COPY",BODY,{"derivedFrom":makeQuery(id+"F9.opPattern","COPY",BODY,{"derivedFrom":makeQuery(id+"F4.opExtrude","SWEPT_BODY",BODY,{"disambiguationData":[OSD([sQuery(id+"F3.wireOp",EDGE,"E615.2"),sQuery(id+"F3.wireOp",EDGE,"E616"),sQuery(id+"F3.wireOp",EDGE,"E617"),sQuery(id+"F3.wireOp",EDGE,"E618")])]}),"instanceName":"1"}),"instanceName":"1"}),"instanceName":"1"});
            transform(context, id + "F12", {"entities" : qUnion([Q0]), "transformType" : TransformType.TRANSLATION_3D, "dx" : 0 * mm, "dy" : 0 * mm, "dz" : -1490.98 * mm, "makeCopy" : true});
        }
        {
            var Q0;
            Q0=makeQuery(id+"F12.opPattern","COPY",BODY,{"derivedFrom":makeQuery(id+"F11.opPattern","COPY",BODY,{"derivedFrom":makeQuery(id+"F10.opPattern","COPY",BODY,{"derivedFrom":makeQuery(id+"F9.opPattern","COPY",BODY,{"derivedFrom":makeQuery(id+"F4.opExtrude","SWEPT_BODY",BODY,{"disambiguationData":[OSD([sQuery(id+"F3.wireOp",EDGE,"E615.2"),sQuery(id+"F3.wireOp",EDGE,"E616"),sQuery(id+"F3.wireOp",EDGE,"E617"),sQuery(id+"F3.wireOp",EDGE,"E618")])]}),"instanceName":"1"}),"instanceName":"1"}),"instanceName":"1"}),"instanceName":"1"});
            transform(context, id + "F13", {"entities" : qUnion([Q0]), "transformType" : TransformType.TRANSLATION_3D, "dx" : 0 * mm, "dy" : 0 * mm, "dz" : -1490.98 * mm, "makeCopy" : true});
        }
        {
            var Q0;
            Q0=makeQuery(id+"F6.opExtrude","SWEPT_BODY",BODY,{"disambiguationData":[OSD([sQuery(id+"F5.wireOp",EDGE,"E619.0"),sQuery(id+"F5.wireOp",EDGE,"E619.1"),sQuery(id+"F5.wireOp",EDGE,"E619.2"),sQuery(id+"F5.wireOp",EDGE,"E619.3")])]});
            transform(context, id + "F14", {"entities" : qUnion([Q0]), "transformType" : TransformType.TRANSLATION_3D, "dx" : 0 * mm, "dy" : 0 * mm, "dz" : -691.13 * mm, "makeCopy" : true});
        }
        {
            var Q0;
            Q0=makeQuery(id+"F14.opPattern","COPY",BODY,{"derivedFrom":makeQuery(id+"F6.opExtrude","SWEPT_BODY",BODY,{"disambiguationData":[OSD([sQuery(id+"F5.wireOp",EDGE,"E619.0"),sQuery(id+"F5.wireOp",EDGE,"E619.1"),sQuery(id+"F5.wireOp",EDGE,"E619.2"),sQuery(id+"F5.wireOp",EDGE,"E619.3")])]}),"instanceName":"1"});
            transform(context, id + "F15", {"entities" : qUnion([Q0]), "transformType" : TransformType.TRANSLATION_3D, "dx" : 0 * mm, "dy" : 0 * mm, "dz" : -1490.98 * mm, "makeCopy" : true});
        }
        {
            var Q0;
            Q0=makeQuery(id+"F15.opPattern","COPY",BODY,{"derivedFrom":makeQuery(id+"F14.opPattern","COPY",BODY,{"derivedFrom":makeQuery(id+"F6.opExtrude","SWEPT_BODY",BODY,{"disambiguationData":[OSD([sQuery(id+"F5.wireOp",EDGE,"E619.0"),sQuery(id+"F5.wireOp",EDGE,"E619.1"),sQuery(id+"F5.wireOp",EDGE,"E619.2"),sQuery(id+"F5.wireOp",EDGE,"E619.3")])]}),"instanceName":"1"}),"instanceName":"1"});
            transform(context, id + "F16", {"entities" : qUnion([Q0]), "transformType" : TransformType.TRANSLATION_3D, "dx" : 0 * mm, "dy" : 0 * mm, "dz" : -1490.98 * mm, "makeCopy" : true});
        }
        {
            var Q0;
            Q0=makeQuery(id+"F16.opPattern","COPY",BODY,{"derivedFrom":makeQuery(id+"F15.opPattern","COPY",BODY,{"derivedFrom":makeQuery(id+"F14.opPattern","COPY",BODY,{"derivedFrom":makeQuery(id+"F6.opExtrude","SWEPT_BODY",BODY,{"disambiguationData":[OSD([sQuery(id+"F5.wireOp",EDGE,"E619.0"),sQuery(id+"F5.wireOp",EDGE,"E619.1"),sQuery(id+"F5.wireOp",EDGE,"E619.2"),sQuery(id+"F5.wireOp",EDGE,"E619.3")])]}),"instanceName":"1"}),"instanceName":"1"}),"instanceName":"1"});
            transform(context, id + "F17", {"entities" : qUnion([Q0]), "transformType" : TransformType.TRANSLATION_3D, "dx" : 0 * mm, "dy" : 0 * mm, "dz" : -1490.98 * mm, "makeCopy" : true});
        }
        {
            var Q0;
            Q0=makeQuery(id+"F17.opPattern","COPY",BODY,{"derivedFrom":makeQuery(id+"F16.opPattern","COPY",BODY,{"derivedFrom":makeQuery(id+"F15.opPattern","COPY",BODY,{"derivedFrom":makeQuery(id+"F14.opPattern","COPY",BODY,{"derivedFrom":makeQuery(id+"F6.opExtrude","SWEPT_BODY",BODY,{"disambiguationData":[OSD([sQuery(id+"F5.wireOp",EDGE,"E619.0"),sQuery(id+"F5.wireOp",EDGE,"E619.1"),sQuery(id+"F5.wireOp",EDGE,"E619.2"),sQuery(id+"F5.wireOp",EDGE,"E619.3")])]}),"instanceName":"1"}),"instanceName":"1"}),"instanceName":"1"}),"instanceName":"1"});
            transform(context, id + "F18", {"entities" : qUnion([Q0]), "transformType" : TransformType.TRANSLATION_3D, "dx" : 0 * mm, "dy" : 0 * mm, "dz" : -1490.98 * mm, "makeCopy" : true});
        }
        {
            var Q0;
            Q0=makeQuery(id+"F9.opPattern","COPY",FACE,{"derivedFrom":makeQuery(id+"F4.opExtrude","SWEPT_FACE",FACE,{"disambiguationData":[OSD([sQuery(id+"F3.wireOp",EDGE,"E615.2")])]}),"instanceName":"1"});
            var sketch = newSketch(context, id + "F19", { "sketchPlane" : qUnion([Q0])});
            skLineSegment(sketch, "E620.0", {"start": v(-560.34, 5382.25) * mm, "end": v(-680.34, 5382.25) * mm});
            skLineSegment(sketch, "E620.1", {"start": v(-689.34, 5405.08) * mm, "end": v(-689.34, 5391.25) * mm});
            skLineSegment(sketch, "E620.2", {"start": v(-551.34, 5405.08) * mm, "end": v(-551.34, 5391.25) * mm});
            skPoint(sketch, "E621.0", {"position": v(-692.09, 5408.25) * mm});
            skPoint(sketch, "E621.1", {"position": v(-548.59, 5408.25) * mm});
            skArc(sketch, "E622", {"start": v(-689.34, 5391.25) * mm, "mid": v(-686.7, 5384.88) * mm, "end": v(-680.34, 5382.25) * mm});
            skArc(sketch, "E623", {"start": v(-560.34, 5382.25) * mm, "mid": v(-553.97, 5384.88) * mm, "end": v(-551.34, 5391.25) * mm});
            skArc(sketch, "E624", {"start": v(-548.59, 5408.25) * mm, "mid": v(-548.6, 5408.25) * mm, "end": v(-548.6, 5408.25) * mm});
            skArc(sketch, "E625", {"start": v(-692.08, 5408.25) * mm, "mid": v(-692.08, 5408.25) * mm, "end": v(-692.09, 5408.25) * mm});
            skLineSegment(sketch, "E626", {"start": v(-692.09, 5408.25) * mm, "end": v(-548.59, 5408.25) * mm});
            skLineSegment(sketch, "E627.0", {"start": v(-170.37, 5408.25) * mm, "end": v(-1070.32, 5408.25) * mm});
            skLineSegment(sketch, "E628.0", {"start": v(-1070.32, 5051.75) * mm, "end": v(-170.37, 5051.75) * mm});
            skLineSegment(sketch, "E629", {"start": v(-1070.48, 5405.08) * mm, "end": v(-689.34, 5405.08) * mm});
            skLineSegment(sketch, "E630", {"start": v(-170.37, 5405.08) * mm, "end": v(-170.37, 5408.25) * mm});
            skLineSegment(sketch, "E631", {"start": v(-170.37, 5051.75) * mm, "end": v(-170.37, 5054.92) * mm});
            skLineSegment(sketch, "E632", {"start": v(-170.37, 5054.92) * mm, "end": v(-1070.32, 5054.92) * mm});
            skPoint(sketch, "E633.orphan", {"position": v(-689.34, 5405.5) * mm});
            skPoint(sketch, "E634.orphan", {"position": v(-551.34, 5405.5) * mm});
            skLineSegment(sketch, "E635.trimOffspring", {"start": v(-551.34, 5405.08) * mm, "end": v(-170.37, 5405.08) * mm});
            skLineSegment(sketch, "E636", {"start": v(-1070.32, 5408.25) * mm, "end": v(-1070.48, 5408.25) * mm});
            skLineSegment(sketch, "E637", {"start": v(-1070.48, 5408.25) * mm, "end": v(-1070.48, 5405.08) * mm});
            skPoint(sketch, "E638.orphan", {"position": v(-170.32, 5408.25) * mm});
            skPoint(sketch, "E639.orphan", {"position": v(-170.32, 5405.08) * mm});
            skPoint(sketch, "E640.orphan", {"position": v(-170.32, 5051.75) * mm});
            skLineSegment(sketch, "E641", {"start": v(-1070.32, 5051.75) * mm, "end": v(-1070.48, 5051.75) * mm});
            skLineSegment(sketch, "E642", {"start": v(-1070.48, 5051.75) * mm, "end": v(-1070.48, 5054.92) * mm});
            skLineSegment(sketch, "E643", {"start": v(-1070.48, 5054.92) * mm, "end": v(-1070.32, 5054.92) * mm});
            skSolve(sketch);
        }
        {
            var Q0;
            Q0 = qSketchRegion(id + "F19", true);
            extrude(context, id + "F20", {"entities" : qUnion([Q0]), "operationType" : NewBodyOperationType.REMOVE, "oppositeDirection" : true, "depth" : 355.6 * mm});
        }
        {
            var Q0;
            Q0=makeQuery(id+"F20.boolean.opBoolean","COPY",FACE,{"derivedFrom":makeQuery(id+"F20.opExtrude","SWEPT_FACE",FACE,{"disambiguationData":[OSD([sQuery(id+"F19.wireOp",EDGE,"E620.1")])]})});
            var Q1;
            Q1=makeQuery(id+"F20.boolean.opBoolean","COPY",FACE,{"derivedFrom":makeQuery(id+"F20.opExtrude","SWEPT_FACE",FACE,{"disambiguationData":[OSD([sQuery(id+"F19.wireOp",EDGE,"E620.0")])]})});
            var Q2;
            Q2=makeQuery(id+"F20.boolean.opBoolean","COPY",FACE,{"derivedFrom":makeQuery(id+"F20.opExtrude","SWEPT_FACE",FACE,{"disambiguationData":[OSD([sQuery(id+"F19.wireOp",EDGE,"E622")])]})});
            var Q3;
            Q3=makeQuery(id+"F20.boolean.opBoolean","COPY",FACE,{"derivedFrom":makeQuery(id+"F20.opExtrude","SWEPT_FACE",FACE,{"disambiguationData":[OSD([sQuery(id+"F19.wireOp",EDGE,"E629")])]})});
            var Q4;
            Q4=makeQuery(id+"F20.boolean.opBoolean","COPY",FACE,{"derivedFrom":makeQuery(id+"F20.opExtrude","SWEPT_FACE",FACE,{"disambiguationData":[OSD([sQuery(id+"F19.wireOp",EDGE,"E623")])]})});
            var Q5;
            Q5=makeQuery(id+"F20.boolean.opBoolean","COPY",FACE,{"derivedFrom":makeQuery(id+"F20.opExtrude","SWEPT_FACE",FACE,{"disambiguationData":[OSD([sQuery(id+"F19.wireOp",EDGE,"E620.2")])]})});
            var Q6;
            Q6=makeQuery(id+"F20.boolean.opBoolean","COPY",FACE,{"derivedFrom":makeQuery(id+"F20.opExtrude","SWEPT_FACE",FACE,{"disambiguationData":[OSD([sQuery(id+"F19.wireOp",EDGE,"E635.trimOffspring")])]})});
            shell(context, id + "F21", {"entities" : qUnion([Q0, Q1, Q2, Q3, Q4, Q5, Q6]), "thickness" : 19.05 * mm});
        }
        {
            var Q0;
            Q0=makeQuery(id+"F10.opPattern","COPY",FACE,{"derivedFrom":makeQuery(id+"F9.opPattern","COPY",FACE,{"derivedFrom":makeQuery(id+"F4.opExtrude","SWEPT_FACE",FACE,{"disambiguationData":[OSD([sQuery(id+"F3.wireOp",EDGE,"E615.2")])]}),"instanceName":"1"}),"instanceName":"1"});
            var sketch = newSketch(context, id + "F22", { "sketchPlane" : qUnion([Q0])});
            skLineSegment(sketch, "E644", {"start": v(-1070.48, 3918.37) * mm, "end": v(-170.37, 3918.37) * mm});
            skLineSegment(sketch, "E645", {"start": v(-170.37, 3918.37) * mm, "end": v(-170.37, 3915.2) * mm});
            skLineSegment(sketch, "E646", {"start": v(-170.37, 3915.2) * mm, "end": v(-1070.48, 3915.2) * mm});
            skLineSegment(sketch, "E647", {"start": v(-1070.48, 3915.2) * mm, "end": v(-1070.48, 3918.37) * mm});
            skLineSegment(sketch, "E648", {"start": v(-1070.48, 3561.83) * mm, "end": v(-170.37, 3561.83) * mm});
            skLineSegment(sketch, "E649", {"start": v(-170.37, 3561.83) * mm, "end": v(-170.37, 3565) * mm});
            skLineSegment(sketch, "E650", {"start": v(-170.37, 3565) * mm, "end": v(-1070.48, 3565) * mm});
            skLineSegment(sketch, "E651", {"start": v(-1070.48, 3565) * mm, "end": v(-1070.48, 3561.83) * mm});
            skSolve(sketch);
        }
        {
            var Q0;
            Q0 = qSketchRegion(id + "F22", true);
            extrude(context, id + "F23", {"entities" : qUnion([Q0]), "operationType" : NewBodyOperationType.REMOVE, "oppositeDirection" : true, "depth" : 355.6 * mm});
        }
        {
            var Q0;
            Q0=makeQuery(id+"F23.boolean.opBoolean","COPY",FACE,{"derivedFrom":makeQuery(id+"F23.opExtrude","SWEPT_FACE",FACE,{"disambiguationData":[OSD([sQuery(id+"F22.wireOp",EDGE,"E646")])]})});
            shell(context, id + "F24", {"entities" : qUnion([Q0]), "thickness" : 19.05 * mm});
        }
        {
            var Q0;
            Q0=makeQuery(id+"F11.opPattern","COPY",FACE,{"derivedFrom":makeQuery(id+"F10.opPattern","COPY",FACE,{"derivedFrom":makeQuery(id+"F9.opPattern","COPY",FACE,{"derivedFrom":makeQuery(id+"F4.opExtrude","SWEPT_FACE",FACE,{"disambiguationData":[OSD([sQuery(id+"F3.wireOp",EDGE,"E615.2")])]}),"instanceName":"1"}),"instanceName":"1"}),"instanceName":"1"});
            var sketch = newSketch(context, id + "F25", { "sketchPlane" : qUnion([Q0])});
            skLineSegment(sketch, "E652.bottom", {"start": v(-1070.48, 2249.53) * mm, "end": v(-170.37, 2249.53) * mm});
            skLineSegment(sketch, "E652.top", {"start": v(-1070.48, 2246.35) * mm, "end": v(-689.4, 2246.35) * mm});
            skLineSegment(sketch, "E652.left", {"start": v(-1070.48, 2249.53) * mm, "end": v(-1070.48, 2246.35) * mm});
            skLineSegment(sketch, "E652.right", {"start": v(-170.37, 2249.53) * mm, "end": v(-170.37, 2246.35) * mm});
            skLineSegment(sketch, "E653", {"start": v(-689.4, 2246.35) * mm, "end": v(-689.4, 2232.56) * mm});
            skLineSegment(sketch, "E654.0", {"start": v(-560.34, 2223.63) * mm, "end": v(-680.34, 2223.63) * mm});
            skLineSegment(sketch, "E655", {"start": v(-551.35, 2246.35) * mm, "end": v(-551.35, 2232.5) * mm});
            skArc(sketch, "E656", {"start": v(-560.34, 2223.63) * mm, "mid": v(-554.02, 2226.22) * mm, "end": v(-551.35, 2232.5) * mm});
            skArc(sketch, "E657", {"start": v(-689.4, 2232.56) * mm, "mid": v(-686.7, 2226.24) * mm, "end": v(-680.34, 2223.63) * mm});
            skLineSegment(sketch, "E658.trimOffspring", {"start": v(-551.35, 2246.35) * mm, "end": v(-170.37, 2246.35) * mm});
            skSolve(sketch);
        }
        {
            var Q0;
            {var subQ0=sQuery(id+"F25.wireOp",EDGE,"E652.bottom");Q0=makeQuery(id+"F25.imprint","IMPRINT",FACE,{"disambiguationData":[TD([[makeQuery(id+"F25.imprint","IMPRINT",EDGE,{"derivedFrom":subQ0}),1.0]])]});}
            var sketch = newSketch(context, id + "F26", { "sketchPlane" : qUnion([Q0])});
            skLineSegment(sketch, "E659.0", {"start": v(-1070.48, 2428.54) * mm, "end": v(-170.37, 2428.54) * mm});
            skLineSegment(sketch, "E659.1", {"start": v(-1070.48, 2425.36) * mm, "end": v(-689.4, 2425.36) * mm});
            skLineSegment(sketch, "E659.2", {"start": v(-1070.48, 2428.54) * mm, "end": v(-1070.48, 2425.36) * mm});
            skLineSegment(sketch, "E659.3", {"start": v(-170.37, 2428.54) * mm, "end": v(-170.37, 2425.36) * mm});
            skLineSegment(sketch, "E659.4", {"start": v(-689.4, 2425.36) * mm, "end": v(-689.4, 2411.57) * mm});
            skLineSegment(sketch, "E659.5", {"start": v(-560.34, 2402.64) * mm, "end": v(-680.34, 2402.64) * mm});
            skLineSegment(sketch, "E659.6", {"start": v(-551.35, 2425.36) * mm, "end": v(-551.35, 2411.52) * mm});
            skArc(sketch, "E659.7", {"start": v(-560.34, 2402.64) * mm, "mid": v(-554.02, 2405.23) * mm, "end": v(-551.35, 2411.52) * mm});
            skArc(sketch, "E659.8", {"start": v(-689.4, 2411.57) * mm, "mid": v(-686.7, 2405.25) * mm, "end": v(-680.34, 2402.64) * mm});
            skLineSegment(sketch, "E659.9", {"start": v(-551.35, 2425.36) * mm, "end": v(-170.37, 2425.36) * mm});
            skSolve(sketch);
        }
        {
            var Q0;
            {var subQ0=sQuery(id+"F3.wireOp",EDGE,"E618");var subQ3=sQuery(id+"F3.wireOp",EDGE,"E615.2");Q0=makeQuery(id+"F28.boolean.opBoolean","SPLIT",FACE,{"disambiguationData":[TD([makeQuery(id+"F11.opPattern","COPY",FACE,{"derivedFrom":makeQuery(id+"F10.opPattern","COPY",FACE,{"derivedFrom":makeQuery(id+"F9.opPattern","COPY",FACE,{"derivedFrom":makeQuery(id+"F4.opExtrude","SWEPT_FACE",FACE,{"disambiguationData":[OSD([subQ0])]}),"instanceName":"1"}),"instanceName":"1"}),"instanceName":"1"})])],"derivedFrom":makeQuery(id+"F11.opPattern","COPY",FACE,{"derivedFrom":makeQuery(id+"F10.opPattern","COPY",FACE,{"derivedFrom":makeQuery(id+"F9.opPattern","COPY",FACE,{"derivedFrom":makeQuery(id+"F4.opExtrude","SWEPT_FACE",FACE,{"disambiguationData":[OSD([subQ3])]}),"instanceName":"1"}),"instanceName":"1"}),"instanceName":"1"})});}
            var sketch = newSketch(context, id + "F27", { "sketchPlane" : qUnion([Q0])});
            skLineSegment(sketch, "E660.bottom", {"start": v(-1070.48, 2072.08) * mm, "end": v(-170.37, 2072.08) * mm});
            skLineSegment(sketch, "E660.top", {"start": v(-1070.48, 2075.25) * mm, "end": v(-170.37, 2075.25) * mm});
            skLineSegment(sketch, "E660.left", {"start": v(-1070.48, 2072.08) * mm, "end": v(-1070.48, 2075.25) * mm});
            skLineSegment(sketch, "E660.right", {"start": v(-170.37, 2072.08) * mm, "end": v(-170.37, 2075.25) * mm});
            skSolve(sketch);
        }
        {
            var Q0;
            Q0 = qSketchRegion(id + "F26", true);
            var Q1;
            Q1 = qSketchRegion(id + "F25", true);
            var Q2;
            Q2 = qSketchRegion(id + "F27", true);
            extrude(context, id + "F28", {"entities" : qUnion([Q0, Q1, Q2]), "operationType" : NewBodyOperationType.REMOVE, "oppositeDirection" : true, "depth" : 355.6 * mm});
        }
        {
            var Q0;
            Q0=makeQuery(id+"F28.boolean.opBoolean","COPY",FACE,{"derivedFrom":makeQuery(id+"F28.opExtrude","SWEPT_FACE",FACE,{"disambiguationData":[OSD([sQuery(id+"F25.wireOp",EDGE,"E654.0")])]})});
            var Q1;
            Q1=makeQuery(id+"F28.boolean.opBoolean","COPY",FACE,{"derivedFrom":makeQuery(id+"F28.opExtrude","SWEPT_FACE",FACE,{"disambiguationData":[OSD([sQuery(id+"F25.wireOp",EDGE,"E656")])]})});
            var Q2;
            Q2=makeQuery(id+"F28.boolean.opBoolean","COPY",FACE,{"derivedFrom":makeQuery(id+"F28.opExtrude","SWEPT_FACE",FACE,{"disambiguationData":[OSD([sQuery(id+"F25.wireOp",EDGE,"E655")])]})});
            var Q3;
            Q3=makeQuery(id+"F28.boolean.opBoolean","COPY",FACE,{"derivedFrom":makeQuery(id+"F28.opExtrude","SWEPT_FACE",FACE,{"disambiguationData":[OSD([sQuery(id+"F25.wireOp",EDGE,"E658.trimOffspring")])]})});
            var Q4;
            Q4=makeQuery(id+"F28.boolean.opBoolean","COPY",FACE,{"derivedFrom":makeQuery(id+"F28.opExtrude","SWEPT_FACE",FACE,{"disambiguationData":[OSD([sQuery(id+"F25.wireOp",EDGE,"E657")])]})});
            var Q5;
            Q5=makeQuery(id+"F28.boolean.opBoolean","COPY",FACE,{"derivedFrom":makeQuery(id+"F28.opExtrude","SWEPT_FACE",FACE,{"disambiguationData":[OSD([sQuery(id+"F25.wireOp",EDGE,"E653")])]})});
            var Q6;
            Q6=makeQuery(id+"F28.boolean.opBoolean","COPY",FACE,{"derivedFrom":makeQuery(id+"F28.opExtrude","SWEPT_FACE",FACE,{"disambiguationData":[OSD([sQuery(id+"F25.wireOp",EDGE,"E652.top")])]})});
            var Q7;
            Q7=makeQuery(id+"F28.boolean.opBoolean","COPY",FACE,{"derivedFrom":makeQuery(id+"F28.opExtrude","SWEPT_FACE",FACE,{"disambiguationData":[OSD([sQuery(id+"F26.wireOp",EDGE,"E659.5")])]})});
            var Q8;
            Q8=makeQuery(id+"F28.boolean.opBoolean","COPY",FACE,{"derivedFrom":makeQuery(id+"F28.opExtrude","SWEPT_FACE",FACE,{"disambiguationData":[OSD([sQuery(id+"F26.wireOp",EDGE,"E659.8")])]})});
            var Q9;
            Q9=makeQuery(id+"F28.boolean.opBoolean","COPY",FACE,{"derivedFrom":makeQuery(id+"F28.opExtrude","SWEPT_FACE",FACE,{"disambiguationData":[OSD([sQuery(id+"F26.wireOp",EDGE,"E659.4")])]})});
            var Q10;
            Q10=makeQuery(id+"F28.boolean.opBoolean","COPY",FACE,{"derivedFrom":makeQuery(id+"F28.opExtrude","SWEPT_FACE",FACE,{"disambiguationData":[OSD([sQuery(id+"F26.wireOp",EDGE,"E659.1")])]})});
            var Q11;
            Q11=makeQuery(id+"F28.boolean.opBoolean","COPY",FACE,{"derivedFrom":makeQuery(id+"F28.opExtrude","SWEPT_FACE",FACE,{"disambiguationData":[OSD([sQuery(id+"F26.wireOp",EDGE,"E659.9")])]})});
            var Q12;
            Q12=makeQuery(id+"F28.boolean.opBoolean","COPY",FACE,{"derivedFrom":makeQuery(id+"F28.opExtrude","SWEPT_FACE",FACE,{"disambiguationData":[OSD([sQuery(id+"F26.wireOp",EDGE,"E659.7")])]})});
            var Q13;
            Q13=makeQuery(id+"F28.boolean.opBoolean","COPY",FACE,{"derivedFrom":makeQuery(id+"F28.opExtrude","SWEPT_FACE",FACE,{"disambiguationData":[OSD([sQuery(id+"F26.wireOp",EDGE,"E659.6")])]})});
            shell(context, id + "F29", {"entities" : qUnion([Q0, Q1, Q2, Q3, Q4, Q5, Q6, Q7, Q8, Q9, Q10, Q11, Q12, Q13]), "thickness" : 19.05 * mm});
        }
        {
            var Q0;
            Q0=makeQuery(id+"F12.opPattern","COPY",FACE,{"derivedFrom":makeQuery(id+"F11.opPattern","COPY",FACE,{"derivedFrom":makeQuery(id+"F10.opPattern","COPY",FACE,{"derivedFrom":makeQuery(id+"F9.opPattern","COPY",FACE,{"derivedFrom":makeQuery(id+"F4.opExtrude","SWEPT_FACE",FACE,{"disambiguationData":[OSD([sQuery(id+"F3.wireOp",EDGE,"E615.2")])]}),"instanceName":"1"}),"instanceName":"1"}),"instanceName":"1"}),"instanceName":"1"});
            var sketch = newSketch(context, id + "F30", { "sketchPlane" : qUnion([Q0])});
            skLineSegment(sketch, "E661.0", {"start": v(-1070.48, 819.1) * mm, "end": v(-170.37, 819.1) * mm});
            skLineSegment(sketch, "E661.1", {"start": v(-1070.48, 815.93) * mm, "end": v(-689.4, 815.93) * mm});
            skLineSegment(sketch, "E661.2", {"start": v(-1070.48, 819.1) * mm, "end": v(-1070.48, 815.93) * mm});
            skLineSegment(sketch, "E661.3", {"start": v(-170.37, 819.1) * mm, "end": v(-170.37, 815.93) * mm});
            skLineSegment(sketch, "E661.4", {"start": v(-689.4, 815.93) * mm, "end": v(-689.4, 802.14) * mm});
            skLineSegment(sketch, "E661.5", {"start": v(-560.34, 793.2) * mm, "end": v(-680.34, 793.2) * mm});
            skLineSegment(sketch, "E661.6", {"start": v(-551.35, 815.93) * mm, "end": v(-551.35, 802.08) * mm});
            skArc(sketch, "E661.7", {"start": v(-560.34, 793.2) * mm, "mid": v(-554.02, 795.8) * mm, "end": v(-551.35, 802.08) * mm});
            skArc(sketch, "E661.8", {"start": v(-689.4, 802.14) * mm, "mid": v(-686.7, 795.81) * mm, "end": v(-680.34, 793.2) * mm});
            skLineSegment(sketch, "E661.9", {"start": v(-551.35, 815.93) * mm, "end": v(-170.37, 815.93) * mm});
            skLineSegment(sketch, "E662.0", {"start": v(-1070.48, 938.05) * mm, "end": v(-170.37, 938.05) * mm});
            skLineSegment(sketch, "E662.1", {"start": v(-1070.48, 934.88) * mm, "end": v(-689.4, 934.88) * mm});
            skLineSegment(sketch, "E662.2", {"start": v(-1070.48, 938.05) * mm, "end": v(-1070.48, 934.88) * mm});
            skLineSegment(sketch, "E662.3", {"start": v(-170.37, 938.05) * mm, "end": v(-170.37, 934.88) * mm});
            skLineSegment(sketch, "E662.4", {"start": v(-689.4, 934.88) * mm, "end": v(-689.4, 921.09) * mm});
            skLineSegment(sketch, "E662.5", {"start": v(-560.34, 912.15) * mm, "end": v(-680.34, 912.15) * mm});
            skLineSegment(sketch, "E662.6", {"start": v(-551.35, 934.88) * mm, "end": v(-551.35, 921.03) * mm});
            skArc(sketch, "E662.7", {"start": v(-560.34, 912.15) * mm, "mid": v(-554.02, 914.75) * mm, "end": v(-551.35, 921.03) * mm});
            skArc(sketch, "E662.8", {"start": v(-689.4, 921.09) * mm, "mid": v(-686.7, 914.76) * mm, "end": v(-680.34, 912.15) * mm});
            skLineSegment(sketch, "E662.9", {"start": v(-551.35, 934.88) * mm, "end": v(-170.37, 934.88) * mm});
            skLineSegment(sketch, "E663.0", {"start": v(-1070.48, 700.06) * mm, "end": v(-170.37, 700.06) * mm});
            skLineSegment(sketch, "E663.1", {"start": v(-1070.48, 696.89) * mm, "end": v(-689.4, 696.89) * mm});
            skLineSegment(sketch, "E663.2", {"start": v(-1070.48, 700.06) * mm, "end": v(-1070.48, 696.89) * mm});
            skLineSegment(sketch, "E663.3", {"start": v(-170.37, 700.06) * mm, "end": v(-170.37, 696.89) * mm});
            skLineSegment(sketch, "E663.4", {"start": v(-689.4, 696.89) * mm, "end": v(-689.4, 683.1) * mm});
            skLineSegment(sketch, "E663.5", {"start": v(-560.34, 674.17) * mm, "end": v(-680.34, 674.17) * mm});
            skLineSegment(sketch, "E663.6", {"start": v(-551.35, 696.89) * mm, "end": v(-551.35, 683.04) * mm});
            skArc(sketch, "E663.7", {"start": v(-560.34, 674.17) * mm, "mid": v(-554.02, 676.76) * mm, "end": v(-551.35, 683.04) * mm});
            skArc(sketch, "E663.8", {"start": v(-689.4, 683.1) * mm, "mid": v(-686.7, 676.77) * mm, "end": v(-680.34, 674.17) * mm});
            skLineSegment(sketch, "E663.9", {"start": v(-551.35, 696.89) * mm, "end": v(-170.37, 696.89) * mm});
            skLineSegment(sketch, "E664.0", {"start": v(-1070.48, 581.92) * mm, "end": v(-170.37, 581.92) * mm});
            skLineSegment(sketch, "E664.1", {"start": v(-1070.48, 585.1) * mm, "end": v(-170.37, 585.1) * mm});
            skLineSegment(sketch, "E664.2", {"start": v(-1070.48, 581.92) * mm, "end": v(-1070.48, 585.1) * mm});
            skLineSegment(sketch, "E664.3", {"start": v(-170.37, 581.92) * mm, "end": v(-170.37, 585.1) * mm});
            skSolve(sketch);
        }
        {
            var Q0;
            Q0 = qSketchRegion(id + "F30", true);
            extrude(context, id + "F31", {"entities" : qUnion([Q0]), "operationType" : NewBodyOperationType.REMOVE, "oppositeDirection" : true, "depth" : 355.6 * mm});
        }
        {
            var Q0;
            Q0=makeQuery(id+"F31.boolean.opBoolean","COPY",FACE,{"derivedFrom":makeQuery(id+"F31.opExtrude","SWEPT_FACE",FACE,{"disambiguationData":[OSD([sQuery(id+"F30.wireOp",EDGE,"E662.5")])]})});
            var Q1;
            Q1=makeQuery(id+"F31.boolean.opBoolean","COPY",FACE,{"derivedFrom":makeQuery(id+"F31.opExtrude","SWEPT_FACE",FACE,{"disambiguationData":[OSD([sQuery(id+"F30.wireOp",EDGE,"E662.7")])]})});
            var Q2;
            Q2=makeQuery(id+"F31.boolean.opBoolean","COPY",FACE,{"derivedFrom":makeQuery(id+"F31.opExtrude","SWEPT_FACE",FACE,{"disambiguationData":[OSD([sQuery(id+"F30.wireOp",EDGE,"E662.6")])]})});
            var Q3;
            Q3=makeQuery(id+"F31.boolean.opBoolean","COPY",FACE,{"derivedFrom":makeQuery(id+"F31.opExtrude","SWEPT_FACE",FACE,{"disambiguationData":[OSD([sQuery(id+"F30.wireOp",EDGE,"E662.9")])]})});
            var Q4;
            Q4=makeQuery(id+"F31.boolean.opBoolean","COPY",FACE,{"derivedFrom":makeQuery(id+"F31.opExtrude","SWEPT_FACE",FACE,{"disambiguationData":[OSD([sQuery(id+"F30.wireOp",EDGE,"E662.8")])]})});
            var Q5;
            Q5=makeQuery(id+"F31.boolean.opBoolean","COPY",FACE,{"derivedFrom":makeQuery(id+"F31.opExtrude","SWEPT_FACE",FACE,{"disambiguationData":[OSD([sQuery(id+"F30.wireOp",EDGE,"E662.4")])]})});
            var Q6;
            Q6=makeQuery(id+"F31.boolean.opBoolean","COPY",FACE,{"derivedFrom":makeQuery(id+"F31.opExtrude","SWEPT_FACE",FACE,{"disambiguationData":[OSD([sQuery(id+"F30.wireOp",EDGE,"E662.1")])]})});
            var Q7;
            Q7=makeQuery(id+"F31.boolean.opBoolean","COPY",FACE,{"derivedFrom":makeQuery(id+"F31.opExtrude","SWEPT_FACE",FACE,{"disambiguationData":[OSD([sQuery(id+"F30.wireOp",EDGE,"E661.8")])]})});
            var Q8;
            Q8=makeQuery(id+"F31.boolean.opBoolean","COPY",FACE,{"derivedFrom":makeQuery(id+"F31.opExtrude","SWEPT_FACE",FACE,{"disambiguationData":[OSD([sQuery(id+"F30.wireOp",EDGE,"E661.4")])]})});
            var Q9;
            Q9=makeQuery(id+"F31.boolean.opBoolean","COPY",FACE,{"derivedFrom":makeQuery(id+"F31.opExtrude","SWEPT_FACE",FACE,{"disambiguationData":[OSD([sQuery(id+"F30.wireOp",EDGE,"E661.1")])]})});
            var Q10;
            Q10=makeQuery(id+"F31.boolean.opBoolean","COPY",FACE,{"derivedFrom":makeQuery(id+"F31.opExtrude","SWEPT_FACE",FACE,{"disambiguationData":[OSD([sQuery(id+"F30.wireOp",EDGE,"E661.5")])]})});
            var Q11;
            Q11=makeQuery(id+"F31.boolean.opBoolean","COPY",FACE,{"derivedFrom":makeQuery(id+"F31.opExtrude","SWEPT_FACE",FACE,{"disambiguationData":[OSD([sQuery(id+"F30.wireOp",EDGE,"E661.7")])]})});
            var Q12;
            Q12=makeQuery(id+"F31.boolean.opBoolean","COPY",FACE,{"derivedFrom":makeQuery(id+"F31.opExtrude","SWEPT_FACE",FACE,{"disambiguationData":[OSD([sQuery(id+"F30.wireOp",EDGE,"E661.6")])]})});
            var Q13;
            Q13=makeQuery(id+"F31.boolean.opBoolean","COPY",FACE,{"derivedFrom":makeQuery(id+"F31.opExtrude","SWEPT_FACE",FACE,{"disambiguationData":[OSD([sQuery(id+"F30.wireOp",EDGE,"E661.9")])]})});
            var Q14;
            Q14=makeQuery(id+"F31.boolean.opBoolean","COPY",FACE,{"derivedFrom":makeQuery(id+"F31.opExtrude","SWEPT_FACE",FACE,{"disambiguationData":[OSD([sQuery(id+"F30.wireOp",EDGE,"E663.5")])]})});
            var Q15;
            Q15=makeQuery(id+"F31.boolean.opBoolean","COPY",FACE,{"derivedFrom":makeQuery(id+"F31.opExtrude","SWEPT_FACE",FACE,{"disambiguationData":[OSD([sQuery(id+"F30.wireOp",EDGE,"E663.7")])]})});
            var Q16;
            Q16=makeQuery(id+"F31.boolean.opBoolean","COPY",FACE,{"derivedFrom":makeQuery(id+"F31.opExtrude","SWEPT_FACE",FACE,{"disambiguationData":[OSD([sQuery(id+"F30.wireOp",EDGE,"E663.6")])]})});
            var Q17;
            Q17=makeQuery(id+"F31.boolean.opBoolean","COPY",FACE,{"derivedFrom":makeQuery(id+"F31.opExtrude","SWEPT_FACE",FACE,{"disambiguationData":[OSD([sQuery(id+"F30.wireOp",EDGE,"E663.9")])]})});
            var Q18;
            Q18=makeQuery(id+"F31.boolean.opBoolean","COPY",FACE,{"derivedFrom":makeQuery(id+"F31.opExtrude","SWEPT_FACE",FACE,{"disambiguationData":[OSD([sQuery(id+"F30.wireOp",EDGE,"E663.8")])]})});
            var Q19;
            Q19=makeQuery(id+"F31.boolean.opBoolean","COPY",FACE,{"derivedFrom":makeQuery(id+"F31.opExtrude","SWEPT_FACE",FACE,{"disambiguationData":[OSD([sQuery(id+"F30.wireOp",EDGE,"E663.4")])]})});
            var Q20;
            Q20=makeQuery(id+"F31.boolean.opBoolean","COPY",FACE,{"derivedFrom":makeQuery(id+"F31.opExtrude","SWEPT_FACE",FACE,{"disambiguationData":[OSD([sQuery(id+"F30.wireOp",EDGE,"E663.1")])]})});
            shell(context, id + "F32", {"entities" : qUnion([Q0, Q1, Q2, Q3, Q4, Q5, Q6, Q7, Q8, Q9, Q10, Q11, Q12, Q13, Q14, Q15, Q16, Q17, Q18, Q19, Q20]), "thickness" : 19.05 * mm});
        }
        {
            var Q0;
            Q0=makeQuery(id+"F13.opPattern","COPY",FACE,{"derivedFrom":makeQuery(id+"F12.opPattern","COPY",FACE,{"derivedFrom":makeQuery(id+"F11.opPattern","COPY",FACE,{"derivedFrom":makeQuery(id+"F10.opPattern","COPY",FACE,{"derivedFrom":makeQuery(id+"F9.opPattern","COPY",FACE,{"derivedFrom":makeQuery(id+"F4.opExtrude","SWEPT_FACE",FACE,{"disambiguationData":[OSD([sQuery(id+"F3.wireOp",EDGE,"E615.2")])]}),"instanceName":"1"}),"instanceName":"1"}),"instanceName":"1"}),"instanceName":"1"}),"instanceName":"1"});
            var sketch = newSketch(context, id + "F33", { "sketchPlane" : qUnion([Q0])});
            skLineSegment(sketch, "E665.bottom", {"start": v(-1070.48, -555.61) * mm, "end": v(-170.37, -555.61) * mm});
            skLineSegment(sketch, "E665.top", {"start": v(-1070.48, -558.79) * mm, "end": v(-170.37, -558.79) * mm});
            skLineSegment(sketch, "E665.left", {"start": v(-1070.48, -555.61) * mm, "end": v(-1070.48, -558.79) * mm});
            skLineSegment(sketch, "E665.right", {"start": v(-170.37, -555.61) * mm, "end": v(-170.37, -558.79) * mm});
            skLineSegment(sketch, "E666.bottom", {"start": v(-1070.48, -912.1) * mm, "end": v(-170.37, -912.1) * mm});
            skLineSegment(sketch, "E666.top", {"start": v(-1070.48, -908.93) * mm, "end": v(-170.37, -908.93) * mm});
            skLineSegment(sketch, "E666.left", {"start": v(-1070.48, -912.1) * mm, "end": v(-1070.48, -908.93) * mm});
            skLineSegment(sketch, "E666.right", {"start": v(-170.37, -912.1) * mm, "end": v(-170.37, -908.93) * mm});
            skSolve(sketch);
        }
        {
            var Q0;
            Q0 = qSketchRegion(id + "F33", true);
            extrude(context, id + "F34", {"entities" : qUnion([Q0]), "operationType" : NewBodyOperationType.REMOVE, "oppositeDirection" : true, "depth" : 355.6 * mm});
        }
        {
            var Q0;
            Q0=makeQuery(id+"F13.opPattern","COPY",FACE,{"derivedFrom":makeQuery(id+"F12.opPattern","COPY",FACE,{"derivedFrom":makeQuery(id+"F11.opPattern","COPY",FACE,{"derivedFrom":makeQuery(id+"F10.opPattern","COPY",FACE,{"derivedFrom":makeQuery(id+"F9.opPattern","COPY",FACE,{"derivedFrom":makeQuery(id+"F4.opExtrude","CAP_FACE",FACE,{"disambiguationData":[OSD([sQuery(id+"F3.wireOp",EDGE,"E615.2"),sQuery(id+"F3.wireOp",EDGE,"E616"),sQuery(id+"F3.wireOp",EDGE,"E617"),sQuery(id+"F3.wireOp",EDGE,"E618")])],"isStart":false}),"instanceName":"1"}),"instanceName":"1"}),"instanceName":"1"}),"instanceName":"1"}),"instanceName":"1"});
            var sketch = newSketch(context, id + "F35", { "sketchPlane" : qUnion([Q0])});
            skLineSegment(sketch, "E667.bottom", {"start": v(8165.5, -908.93) * mm, "end": v(8184.55, -908.93) * mm});
            skLineSegment(sketch, "E667.top", {"start": v(8165.5, -883.53) * mm, "end": v(8168.32, -883.53) * mm});
            skLineSegment(sketch, "E667.left", {"start": v(8165.5, -908.93) * mm, "end": v(8165.5, -883.53) * mm});
            skLineSegment(sketch, "E667.right", {"start": v(8184.55, -908.93) * mm, "end": v(8184.55, -883.53) * mm});
            skArc(sketch, "E668", {"start": v(8184.55, -883.53) * mm, "mid": v(8176.43, -875.41) * mm, "end": v(8168.32, -883.53) * mm});
            skSolve(sketch);
        }
        {
            var Q0;
            Q0 = qSketchRegion(id + "F35", true);
            extrude(context, id + "F36", {"entities" : qUnion([Q0]), "operationType" : NewBodyOperationType.REMOVE, "oppositeDirection" : true, "depth" : 2540 * mm, "hasSecondDirection" : true, "secondDirectionOppositeDirection" : false, "secondDirectionDepth" : 2540 * mm});
        }
        {
            var Q0;
            Q0=makeQuery(id+"F34.boolean.opBoolean","COPY",FACE,{"derivedFrom":makeQuery(id+"F34.opExtrude","SWEPT_FACE",FACE,{"disambiguationData":[OSD([sQuery(id+"F33.wireOp",EDGE,"E665.top")])]})});
            shell(context, id + "F37", {"entities" : qUnion([Q0]), "thickness" : 19.05 * mm});
        }
        {
            var Q0;
            Q0=makeQuery(id+"F14.opPattern","COPY",FACE,{"derivedFrom":makeQuery(id+"F6.opExtrude","SWEPT_FACE",FACE,{"disambiguationData":[OSD([sQuery(id+"F5.wireOp",EDGE,"E619.0")])]}),"instanceName":"1"});
            var sketch = newSketch(context, id + "F38", { "sketchPlane" : qUnion([Q0])});
            skLineSegment(sketch, "E669.bottom", {"start": v(1275.5, 5408.2) * mm, "end": v(1929.55, 5408.2) * mm});
            skLineSegment(sketch, "E669.top", {"start": v(1275.5, 5405.02) * mm, "end": v(1533.15, 5405.02) * mm});
            skLineSegment(sketch, "E669.left", {"start": v(1275.5, 5408.2) * mm, "end": v(1275.5, 5405.02) * mm});
            skLineSegment(sketch, "E669.right", {"start": v(1929.55, 5408.2) * mm, "end": v(1929.55, 5405.02) * mm});
            skLineSegment(sketch, "E670", {"start": v(1533.15, 5405.02) * mm, "end": v(1533.15, 5391.17) * mm});
            skLineSegment(sketch, "E671", {"start": v(1671.17, 5405.02) * mm, "end": v(1671.17, 5391.19) * mm});
            skLineSegment(sketch, "E672.0", {"start": v(1662.16, 5382.25) * mm, "end": v(1542.16, 5382.25) * mm});
            skArc(sketch, "E673", {"start": v(1662.16, 5382.25) * mm, "mid": v(1668.53, 5384.84) * mm, "end": v(1671.17, 5391.19) * mm});
            skArc(sketch, "E674", {"start": v(1533.15, 5391.17) * mm, "mid": v(1535.82, 5384.86) * mm, "end": v(1542.16, 5382.25) * mm});
            skLineSegment(sketch, "E675.trimOffspring", {"start": v(1671.17, 5405.02) * mm, "end": v(1929.55, 5405.02) * mm});
            skLineSegment(sketch, "E676.bottom", {"start": v(1275.5, 5051.83) * mm, "end": v(1929.55, 5051.83) * mm});
            skLineSegment(sketch, "E676.top", {"start": v(1275.5, 5055) * mm, "end": v(1929.55, 5055) * mm});
            skLineSegment(sketch, "E676.left", {"start": v(1275.5, 5051.83) * mm, "end": v(1275.5, 5055) * mm});
            skLineSegment(sketch, "E676.right", {"start": v(1929.55, 5051.83) * mm, "end": v(1929.55, 5055) * mm});
            skSolve(sketch);
        }
        {
            var Q0;
            Q0 = qSketchRegion(id + "F38", true);
            extrude(context, id + "F39", {"entities" : qUnion([Q0]), "operationType" : NewBodyOperationType.REMOVE, "oppositeDirection" : true, "depth" : 355.6 * mm});
        }
        {
            var Q0;
            Q0=makeQuery(id+"F39.boolean.opBoolean","COPY",FACE,{"derivedFrom":makeQuery(id+"F39.opExtrude","SWEPT_FACE",FACE,{"disambiguationData":[OSD([sQuery(id+"F38.wireOp",EDGE,"E670")])]})});
            var Q1;
            Q1=makeQuery(id+"F39.boolean.opBoolean","COPY",FACE,{"derivedFrom":makeQuery(id+"F39.opExtrude","SWEPT_FACE",FACE,{"disambiguationData":[OSD([sQuery(id+"F38.wireOp",EDGE,"E674")])]})});
            var Q2;
            Q2=makeQuery(id+"F39.boolean.opBoolean","COPY",FACE,{"derivedFrom":makeQuery(id+"F39.opExtrude","SWEPT_FACE",FACE,{"disambiguationData":[OSD([sQuery(id+"F38.wireOp",EDGE,"E669.top")])]})});
            var Q3;
            Q3=makeQuery(id+"F39.boolean.opBoolean","COPY",FACE,{"derivedFrom":makeQuery(id+"F39.opExtrude","SWEPT_FACE",FACE,{"disambiguationData":[OSD([sQuery(id+"F38.wireOp",EDGE,"E672.0")])]})});
            var Q4;
            Q4=makeQuery(id+"F39.boolean.opBoolean","COPY",FACE,{"derivedFrom":makeQuery(id+"F39.opExtrude","SWEPT_FACE",FACE,{"disambiguationData":[OSD([sQuery(id+"F38.wireOp",EDGE,"E673")])]})});
            var Q5;
            Q5=makeQuery(id+"F39.boolean.opBoolean","COPY",FACE,{"derivedFrom":makeQuery(id+"F39.opExtrude","SWEPT_FACE",FACE,{"disambiguationData":[OSD([sQuery(id+"F38.wireOp",EDGE,"E671")])]})});
            var Q6;
            Q6=makeQuery(id+"F39.boolean.opBoolean","COPY",FACE,{"derivedFrom":makeQuery(id+"F39.opExtrude","SWEPT_FACE",FACE,{"disambiguationData":[OSD([sQuery(id+"F38.wireOp",EDGE,"E675.trimOffspring")])]})});
            shell(context, id + "F40", {"entities" : qUnion([Q0, Q1, Q2, Q3, Q4, Q5, Q6]), "thickness" : 19.05 * mm});
        }
        {
            var Q0;
            Q0=makeQuery(id+"F15.opPattern","COPY",FACE,{"derivedFrom":makeQuery(id+"F14.opPattern","COPY",FACE,{"derivedFrom":makeQuery(id+"F6.opExtrude","SWEPT_FACE",FACE,{"disambiguationData":[OSD([sQuery(id+"F5.wireOp",EDGE,"E619.0")])]}),"instanceName":"1"}),"instanceName":"1"});
            var sketch = newSketch(context, id + "F41", { "sketchPlane" : qUnion([Q0])});
            skLineSegment(sketch, "E677.bottom", {"start": v(1275.5, 3918.02) * mm, "end": v(1929.55, 3918.02) * mm});
            skLineSegment(sketch, "E677.top", {"start": v(1275.5, 3914.84) * mm, "end": v(1929.55, 3914.84) * mm});
            skLineSegment(sketch, "E677.left", {"start": v(1275.5, 3918.02) * mm, "end": v(1275.5, 3914.84) * mm});
            skLineSegment(sketch, "E677.right", {"start": v(1929.55, 3918.02) * mm, "end": v(1929.55, 3914.84) * mm});
            skLineSegment(sketch, "E678.bottom", {"start": v(1275.5, 3561.76) * mm, "end": v(1929.55, 3561.76) * mm});
            skLineSegment(sketch, "E678.top", {"start": v(1275.5, 3564.94) * mm, "end": v(1929.55, 3564.94) * mm});
            skLineSegment(sketch, "E678.left", {"start": v(1275.5, 3561.76) * mm, "end": v(1275.5, 3564.94) * mm});
            skLineSegment(sketch, "E678.right", {"start": v(1929.55, 3561.76) * mm, "end": v(1929.55, 3564.94) * mm});
            skSolve(sketch);
        }
        {
            var Q0;
            Q0 = qSketchRegion(id + "F41", true);
            extrude(context, id + "F42", {"entities" : qUnion([Q0]), "operationType" : NewBodyOperationType.REMOVE, "oppositeDirection" : true, "depth" : 355.6 * mm});
        }
        {
            var Q0;
            Q0=makeQuery(id+"F42.boolean.opBoolean","COPY",FACE,{"derivedFrom":makeQuery(id+"F42.opExtrude","SWEPT_FACE",FACE,{"disambiguationData":[OSD([sQuery(id+"F41.wireOp",EDGE,"E677.top")])]})});
            shell(context, id + "F43", {"entities" : qUnion([Q0]), "thickness" : 19.05 * mm});
        }
        {
            var Q0;
            Q0=makeQuery(id+"F16.opPattern","COPY",FACE,{"derivedFrom":makeQuery(id+"F15.opPattern","COPY",FACE,{"derivedFrom":makeQuery(id+"F14.opPattern","COPY",FACE,{"derivedFrom":makeQuery(id+"F6.opExtrude","SWEPT_FACE",FACE,{"disambiguationData":[OSD([sQuery(id+"F5.wireOp",EDGE,"E619.0")])]}),"instanceName":"1"}),"instanceName":"1"}),"instanceName":"1"});
            var sketch = newSketch(context, id + "F44", { "sketchPlane" : qUnion([Q0])});
            skLineSegment(sketch, "E679.bottom", {"start": v(1275.5, 2427.44) * mm, "end": v(1929.55, 2427.44) * mm});
            skLineSegment(sketch, "E679.top", {"start": v(1275.5, 2424.27) * mm, "end": v(1532.83, 2424.27) * mm});
            skLineSegment(sketch, "E679.left", {"start": v(1275.5, 2427.44) * mm, "end": v(1275.5, 2424.27) * mm});
            skLineSegment(sketch, "E679.right", {"start": v(1929.55, 2427.44) * mm, "end": v(1929.55, 2424.27) * mm});
            skLineSegment(sketch, "E680", {"start": v(1532.83, 2424.27) * mm, "end": v(1532.83, 2411.01) * mm});
            skLineSegment(sketch, "E681.0", {"start": v(1662.16, 2402.25) * mm, "end": v(1542.16, 2402.25) * mm});
            skLineSegment(sketch, "E682", {"start": v(1671.11, 2424.27) * mm, "end": v(1671.11, 2411.01) * mm});
            skArc(sketch, "E683", {"start": v(1662.16, 2402.25) * mm, "mid": v(1668.48, 2404.75) * mm, "end": v(1671.11, 2411.01) * mm});
            skArc(sketch, "E684", {"start": v(1532.83, 2411.01) * mm, "mid": v(1535.76, 2404.78) * mm, "end": v(1542.16, 2402.25) * mm});
            skLineSegment(sketch, "E685.trimOffspring", {"start": v(1671.11, 2424.27) * mm, "end": v(1929.55, 2424.27) * mm});
            skSolve(sketch);
        }
        {
            var Q0;
            {var subQ0=sQuery(id+"F44.wireOp",EDGE,"E679.top");Q0=makeQuery(id+"F44.imprint","IMPRINT",FACE,{"disambiguationData":[TD([[makeQuery(id+"F44.imprint","IMPRINT",EDGE,{"derivedFrom":subQ0}),-1.0]])]});}
            var sketch = newSketch(context, id + "F45", { "sketchPlane" : qUnion([Q0])});
            skLineSegment(sketch, "E686.0", {"start": v(1267.08, 2249.8) * mm, "end": v(1929.55, 2249.8) * mm});
            skLineSegment(sketch, "E686.1", {"start": v(1267.08, 2246.6) * mm, "end": v(1527.73, 2246.6) * mm});
            skLineSegment(sketch, "E686.2", {"start": v(1267.08, 2249.8) * mm, "end": v(1267.08, 2246.6) * mm});
            skLineSegment(sketch, "E686.3", {"start": v(1929.55, 2249.8) * mm, "end": v(1929.55, 2246.6) * mm});
            skLineSegment(sketch, "E686.4", {"start": v(1527.73, 2246.6) * mm, "end": v(1527.73, 2233.16) * mm});
            skLineSegment(sketch, "E686.5", {"start": v(1658.72, 2224.29) * mm, "end": v(1537.18, 2224.29) * mm});
            skLineSegment(sketch, "E686.6", {"start": v(1667.79, 2246.6) * mm, "end": v(1667.79, 2233.16) * mm});
            skArc(sketch, "E686.7", {"start": v(1658.72, 2224.29) * mm, "mid": v(1665.12, 2226.82) * mm, "end": v(1667.79, 2233.16) * mm});
            skArc(sketch, "E686.8", {"start": v(1527.73, 2233.16) * mm, "mid": v(1530.7, 2226.85) * mm, "end": v(1537.18, 2224.29) * mm});
            skLineSegment(sketch, "E686.9", {"start": v(1667.79, 2246.6) * mm, "end": v(1929.55, 2246.6) * mm});
            skLineSegment(sketch, "E687.bottom", {"start": v(1275.5, 2071.75) * mm, "end": v(1929.64, 2071.75) * mm});
            skLineSegment(sketch, "E687.top", {"start": v(1275.5, 2074.92) * mm, "end": v(1929.64, 2074.92) * mm});
            skLineSegment(sketch, "E687.left", {"start": v(1275.5, 2071.75) * mm, "end": v(1275.5, 2074.92) * mm});
            skLineSegment(sketch, "E687.right", {"start": v(1929.64, 2071.75) * mm, "end": v(1929.64, 2074.92) * mm});
            skSolve(sketch);
        }
        {
            var Q0;
            Q0 = qSketchRegion(id + "F45", true);
            var Q1;
            Q1 = qSketchRegion(id + "F44", true);
            extrude(context, id + "F46", {"entities" : qUnion([Q0, Q1]), "operationType" : NewBodyOperationType.REMOVE, "oppositeDirection" : true, "depth" : 355.6 * mm});
        }
        {
            var Q0;
            Q0=makeQuery(id+"F46.boolean.opBoolean","COPY",FACE,{"derivedFrom":makeQuery(id+"F46.opExtrude","SWEPT_FACE",FACE,{"disambiguationData":[OSD([sQuery(id+"F44.wireOp",EDGE,"E680")])]})});
            var Q1;
            Q1=makeQuery(id+"F46.boolean.opBoolean","COPY",FACE,{"derivedFrom":makeQuery(id+"F46.opExtrude","SWEPT_FACE",FACE,{"disambiguationData":[OSD([sQuery(id+"F44.wireOp",EDGE,"E684")])]})});
            var Q2;
            Q2=makeQuery(id+"F46.boolean.opBoolean","COPY",FACE,{"derivedFrom":makeQuery(id+"F46.opExtrude","SWEPT_FACE",FACE,{"disambiguationData":[OSD([sQuery(id+"F44.wireOp",EDGE,"E681.0")])]})});
            var Q3;
            Q3=makeQuery(id+"F46.boolean.opBoolean","COPY",FACE,{"derivedFrom":makeQuery(id+"F46.opExtrude","SWEPT_FACE",FACE,{"disambiguationData":[OSD([sQuery(id+"F44.wireOp",EDGE,"E679.top")])]})});
            var Q4;
            Q4=makeQuery(id+"F46.boolean.opBoolean","COPY",FACE,{"derivedFrom":makeQuery(id+"F46.opExtrude","SWEPT_FACE",FACE,{"disambiguationData":[OSD([sQuery(id+"F44.wireOp",EDGE,"E683")])]})});
            var Q5;
            Q5=makeQuery(id+"F46.boolean.opBoolean","COPY",FACE,{"derivedFrom":makeQuery(id+"F46.opExtrude","SWEPT_FACE",FACE,{"disambiguationData":[OSD([sQuery(id+"F44.wireOp",EDGE,"E682")])]})});
            var Q6;
            Q6=makeQuery(id+"F46.boolean.opBoolean","COPY",FACE,{"derivedFrom":makeQuery(id+"F46.opExtrude","SWEPT_FACE",FACE,{"disambiguationData":[OSD([sQuery(id+"F44.wireOp",EDGE,"E685.trimOffspring")])]})});
            var Q7;
            Q7=makeQuery(id+"F46.boolean.opBoolean","COPY",FACE,{"derivedFrom":makeQuery(id+"F46.opExtrude","SWEPT_FACE",FACE,{"disambiguationData":[OSD([sQuery(id+"F45.wireOp",EDGE,"E686.5")])]})});
            var Q8;
            Q8=makeQuery(id+"F46.boolean.opBoolean","COPY",FACE,{"derivedFrom":makeQuery(id+"F46.opExtrude","SWEPT_FACE",FACE,{"disambiguationData":[OSD([sQuery(id+"F45.wireOp",EDGE,"E686.7")])]})});
            var Q9;
            Q9=makeQuery(id+"F46.boolean.opBoolean","COPY",FACE,{"derivedFrom":makeQuery(id+"F46.opExtrude","SWEPT_FACE",FACE,{"disambiguationData":[OSD([sQuery(id+"F45.wireOp",EDGE,"E686.6")])]})});
            var Q10;
            Q10=makeQuery(id+"F46.boolean.opBoolean","COPY",FACE,{"derivedFrom":makeQuery(id+"F46.opExtrude","SWEPT_FACE",FACE,{"disambiguationData":[OSD([sQuery(id+"F45.wireOp",EDGE,"E686.9")])]})});
            var Q11;
            Q11=makeQuery(id+"F46.boolean.opBoolean","COPY",FACE,{"derivedFrom":makeQuery(id+"F46.opExtrude","SWEPT_FACE",FACE,{"disambiguationData":[OSD([sQuery(id+"F45.wireOp",EDGE,"E686.8")])]})});
            var Q12;
            Q12=makeQuery(id+"F46.boolean.opBoolean","COPY",FACE,{"derivedFrom":makeQuery(id+"F46.opExtrude","SWEPT_FACE",FACE,{"disambiguationData":[OSD([sQuery(id+"F45.wireOp",EDGE,"E686.4")])]})});
            var Q13;
            Q13=makeQuery(id+"F46.boolean.opBoolean","COPY",FACE,{"derivedFrom":makeQuery(id+"F46.opExtrude","SWEPT_FACE",FACE,{"disambiguationData":[OSD([sQuery(id+"F45.wireOp",EDGE,"E686.1")])]})});
            shell(context, id + "F47", {"entities" : qUnion([Q0, Q1, Q2, Q3, Q4, Q5, Q6, Q7, Q8, Q9, Q10, Q11, Q12, Q13]), "thickness" : 19.05 * mm});
        }
        {
            var Q0;
            Q0=makeQuery(id+"F17.opPattern","COPY",FACE,{"derivedFrom":makeQuery(id+"F16.opPattern","COPY",FACE,{"derivedFrom":makeQuery(id+"F15.opPattern","COPY",FACE,{"derivedFrom":makeQuery(id+"F14.opPattern","COPY",FACE,{"derivedFrom":makeQuery(id+"F6.opExtrude","SWEPT_FACE",FACE,{"disambiguationData":[OSD([sQuery(id+"F5.wireOp",EDGE,"E619.0")])]}),"instanceName":"1"}),"instanceName":"1"}),"instanceName":"1"}),"instanceName":"1"});
            var sketch = newSketch(context, id + "F48", { "sketchPlane" : qUnion([Q0])});
            skLineSegment(sketch, "E688.0", {"start": v(1275.5, 936.47) * mm, "end": v(1929.55, 936.47) * mm});
            skLineSegment(sketch, "E688.1", {"start": v(1275.5, 933.3) * mm, "end": v(1532.83, 933.3) * mm});
            skLineSegment(sketch, "E688.2", {"start": v(1275.5, 936.47) * mm, "end": v(1275.5, 933.3) * mm});
            skLineSegment(sketch, "E688.3", {"start": v(1929.55, 936.47) * mm, "end": v(1929.55, 933.3) * mm});
            skLineSegment(sketch, "E688.4", {"start": v(1532.83, 933.3) * mm, "end": v(1532.83, 920.04) * mm});
            skLineSegment(sketch, "E688.5", {"start": v(1662.16, 911.27) * mm, "end": v(1542.16, 911.27) * mm});
            skLineSegment(sketch, "E688.6", {"start": v(1671.11, 933.3) * mm, "end": v(1671.11, 920.04) * mm});
            skArc(sketch, "E688.7", {"start": v(1662.16, 911.27) * mm, "mid": v(1668.48, 913.77) * mm, "end": v(1671.11, 920.04) * mm});
            skArc(sketch, "E688.8", {"start": v(1532.83, 920.04) * mm, "mid": v(1535.76, 913.8) * mm, "end": v(1542.16, 911.27) * mm});
            skLineSegment(sketch, "E688.9", {"start": v(1671.11, 933.3) * mm, "end": v(1929.55, 933.3) * mm});
            skLineSegment(sketch, "E689.0", {"start": v(-1070.48, 2249.53) * mm, "end": v(-170.37, 2249.53) * mm});
            skLineSegment(sketch, "E689.1", {"start": v(-1070.48, 2246.35) * mm, "end": v(-689.4, 2246.35) * mm});
            skLineSegment(sketch, "E689.2", {"start": v(-1070.48, 2249.53) * mm, "end": v(-1070.48, 2246.35) * mm});
            skLineSegment(sketch, "E689.3", {"start": v(-170.37, 2249.53) * mm, "end": v(-170.37, 2246.35) * mm});
            skLineSegment(sketch, "E689.4", {"start": v(-689.4, 2246.35) * mm, "end": v(-689.4, 2232.56) * mm});
            skLineSegment(sketch, "E689.5", {"start": v(-560.34, 2223.63) * mm, "end": v(-680.34, 2223.63) * mm});
            skLineSegment(sketch, "E689.6", {"start": v(-551.35, 2246.35) * mm, "end": v(-551.35, 2232.5) * mm});
            skArc(sketch, "E689.7", {"start": v(-560.34, 2223.63) * mm, "mid": v(-554.02, 2226.22) * mm, "end": v(-551.35, 2232.5) * mm});
            skArc(sketch, "E689.8", {"start": v(-689.4, 2232.56) * mm, "mid": v(-686.7, 2226.24) * mm, "end": v(-680.34, 2223.63) * mm});
            skLineSegment(sketch, "E689.9", {"start": v(-551.35, 2246.35) * mm, "end": v(-170.37, 2246.35) * mm});
            skLineSegment(sketch, "E689.10", {"start": v(1275.5, 818.62) * mm, "end": v(1929.55, 818.62) * mm});
            skLineSegment(sketch, "E689.11", {"start": v(1275.5, 815.45) * mm, "end": v(1532.83, 815.45) * mm});
            skLineSegment(sketch, "E689.12", {"start": v(1275.5, 818.62) * mm, "end": v(1275.5, 815.45) * mm});
            skLineSegment(sketch, "E689.13", {"start": v(1929.55, 818.62) * mm, "end": v(1929.55, 815.45) * mm});
            skLineSegment(sketch, "E689.14", {"start": v(1532.83, 815.45) * mm, "end": v(1532.83, 802.2) * mm});
            skLineSegment(sketch, "E689.15", {"start": v(1662.16, 793.43) * mm, "end": v(1542.16, 793.43) * mm});
            skLineSegment(sketch, "E689.16", {"start": v(1671.11, 815.45) * mm, "end": v(1671.11, 802.2) * mm});
            skArc(sketch, "E689.17", {"start": v(1662.16, 793.43) * mm, "mid": v(1668.48, 795.93) * mm, "end": v(1671.11, 802.2) * mm});
            skArc(sketch, "E689.18", {"start": v(1532.83, 802.2) * mm, "mid": v(1535.76, 795.96) * mm, "end": v(1542.16, 793.43) * mm});
            skLineSegment(sketch, "E689.19", {"start": v(1671.11, 815.45) * mm, "end": v(1929.55, 815.45) * mm});
            skLineSegment(sketch, "E690.0", {"start": v(1275.5, 700.3) * mm, "end": v(1929.55, 700.3) * mm});
            skLineSegment(sketch, "E690.1", {"start": v(1275.5, 697.13) * mm, "end": v(1532.83, 697.13) * mm});
            skLineSegment(sketch, "E690.2", {"start": v(1275.5, 700.3) * mm, "end": v(1275.5, 697.13) * mm});
            skLineSegment(sketch, "E690.3", {"start": v(1929.55, 700.3) * mm, "end": v(1929.55, 697.13) * mm});
            skLineSegment(sketch, "E690.4", {"start": v(1532.83, 697.13) * mm, "end": v(1532.83, 683.87) * mm});
            skLineSegment(sketch, "E690.5", {"start": v(1662.16, 675.11) * mm, "end": v(1542.16, 675.11) * mm});
            skLineSegment(sketch, "E690.6", {"start": v(1671.11, 697.13) * mm, "end": v(1671.11, 683.87) * mm});
            skArc(sketch, "E690.7", {"start": v(1662.16, 675.11) * mm, "mid": v(1668.48, 677.61) * mm, "end": v(1671.11, 683.87) * mm});
            skArc(sketch, "E690.8", {"start": v(1532.83, 683.87) * mm, "mid": v(1535.76, 677.64) * mm, "end": v(1542.16, 675.11) * mm});
            skLineSegment(sketch, "E690.9", {"start": v(1671.11, 697.13) * mm, "end": v(1929.55, 697.13) * mm});
            skLineSegment(sketch, "E691.0", {"start": v(1275.5, 955.46) * mm, "end": v(1275.5, 560.98) * mm});
            skLineSegment(sketch, "E692.bottom", {"start": v(1275.5, 583.15) * mm, "end": v(1929.55, 583.15) * mm});
            skLineSegment(sketch, "E692.top", {"start": v(1275.5, 579.98) * mm, "end": v(1929.55, 579.98) * mm});
            skLineSegment(sketch, "E692.left", {"start": v(1275.5, 583.15) * mm, "end": v(1275.5, 579.98) * mm});
            skLineSegment(sketch, "E692.right", {"start": v(1929.55, 583.15) * mm, "end": v(1929.55, 579.98) * mm});
            skSolve(sketch);
        }
        {
            var Q0;
            Q0 = qSketchRegion(id + "F48", true);
            extrude(context, id + "F49", {"entities" : qUnion([Q0]), "operationType" : NewBodyOperationType.REMOVE, "oppositeDirection" : true, "depth" : 355.6 * mm});
        }
        {
            var Q0;
            Q0=makeQuery(id+"F49.boolean.opBoolean","COPY",FACE,{"derivedFrom":makeQuery(id+"F49.opExtrude","SWEPT_FACE",FACE,{"disambiguationData":[OSD([sQuery(id+"F48.wireOp",EDGE,"E690.5")])]})});
            var Q1;
            Q1=makeQuery(id+"F49.boolean.opBoolean","COPY",FACE,{"derivedFrom":makeQuery(id+"F49.opExtrude","SWEPT_FACE",FACE,{"disambiguationData":[OSD([sQuery(id+"F48.wireOp",EDGE,"E690.7")])]})});
            var Q2;
            Q2=makeQuery(id+"F49.boolean.opBoolean","COPY",FACE,{"derivedFrom":makeQuery(id+"F49.opExtrude","SWEPT_FACE",FACE,{"disambiguationData":[OSD([sQuery(id+"F48.wireOp",EDGE,"E690.6")])]})});
            var Q3;
            Q3=makeQuery(id+"F49.boolean.opBoolean","COPY",FACE,{"derivedFrom":makeQuery(id+"F49.opExtrude","SWEPT_FACE",FACE,{"disambiguationData":[OSD([sQuery(id+"F48.wireOp",EDGE,"E690.9")])]})});
            var Q4;
            Q4=makeQuery(id+"F49.boolean.opBoolean","COPY",FACE,{"derivedFrom":makeQuery(id+"F49.opExtrude","SWEPT_FACE",FACE,{"disambiguationData":[OSD([sQuery(id+"F48.wireOp",EDGE,"E690.8")])]})});
            var Q5;
            Q5=makeQuery(id+"F49.boolean.opBoolean","COPY",FACE,{"derivedFrom":makeQuery(id+"F49.opExtrude","SWEPT_FACE",FACE,{"disambiguationData":[OSD([sQuery(id+"F48.wireOp",EDGE,"E690.4")])]})});
            var Q6;
            Q6=makeQuery(id+"F49.boolean.opBoolean","COPY",FACE,{"derivedFrom":makeQuery(id+"F49.opExtrude","SWEPT_FACE",FACE,{"disambiguationData":[OSD([sQuery(id+"F48.wireOp",EDGE,"E690.1")])]})});
            var Q7;
            Q7=makeQuery(id+"F49.boolean.opBoolean","COPY",FACE,{"derivedFrom":makeQuery(id+"F49.opExtrude","SWEPT_FACE",FACE,{"disambiguationData":[OSD([sQuery(id+"F48.wireOp",EDGE,"E689.15")])]})});
            var Q8;
            Q8=makeQuery(id+"F49.boolean.opBoolean","COPY",FACE,{"derivedFrom":makeQuery(id+"F49.opExtrude","SWEPT_FACE",FACE,{"disambiguationData":[OSD([sQuery(id+"F48.wireOp",EDGE,"E689.18")])]})});
            var Q9;
            Q9=makeQuery(id+"F49.boolean.opBoolean","COPY",FACE,{"derivedFrom":makeQuery(id+"F49.opExtrude","SWEPT_FACE",FACE,{"disambiguationData":[OSD([sQuery(id+"F48.wireOp",EDGE,"E689.14")])]})});
            var Q10;
            Q10=makeQuery(id+"F49.boolean.opBoolean","COPY",FACE,{"derivedFrom":makeQuery(id+"F49.opExtrude","SWEPT_FACE",FACE,{"disambiguationData":[OSD([sQuery(id+"F48.wireOp",EDGE,"E689.11")])]})});
            var Q11;
            Q11=makeQuery(id+"F49.boolean.opBoolean","COPY",FACE,{"derivedFrom":makeQuery(id+"F49.opExtrude","SWEPT_FACE",FACE,{"disambiguationData":[OSD([sQuery(id+"F48.wireOp",EDGE,"E689.19")])]})});
            var Q12;
            Q12=makeQuery(id+"F49.boolean.opBoolean","COPY",FACE,{"derivedFrom":makeQuery(id+"F49.opExtrude","SWEPT_FACE",FACE,{"disambiguationData":[OSD([sQuery(id+"F48.wireOp",EDGE,"E689.17")])]})});
            var Q13;
            Q13=makeQuery(id+"F49.boolean.opBoolean","COPY",FACE,{"derivedFrom":makeQuery(id+"F49.opExtrude","SWEPT_FACE",FACE,{"disambiguationData":[OSD([sQuery(id+"F48.wireOp",EDGE,"E689.16")])]})});
            var Q14;
            Q14=makeQuery(id+"F49.boolean.opBoolean","COPY",FACE,{"derivedFrom":makeQuery(id+"F49.opExtrude","SWEPT_FACE",FACE,{"disambiguationData":[OSD([sQuery(id+"F48.wireOp",EDGE,"E688.5")])]})});
            var Q15;
            Q15=makeQuery(id+"F49.boolean.opBoolean","COPY",FACE,{"derivedFrom":makeQuery(id+"F49.opExtrude","SWEPT_FACE",FACE,{"disambiguationData":[OSD([sQuery(id+"F48.wireOp",EDGE,"E688.7")])]})});
            var Q16;
            Q16=makeQuery(id+"F49.boolean.opBoolean","COPY",FACE,{"derivedFrom":makeQuery(id+"F49.opExtrude","SWEPT_FACE",FACE,{"disambiguationData":[OSD([sQuery(id+"F48.wireOp",EDGE,"E688.6")])]})});
            var Q17;
            Q17=makeQuery(id+"F49.boolean.opBoolean","COPY",FACE,{"derivedFrom":makeQuery(id+"F49.opExtrude","SWEPT_FACE",FACE,{"disambiguationData":[OSD([sQuery(id+"F48.wireOp",EDGE,"E688.9")])]})});
            var Q18;
            Q18=makeQuery(id+"F49.boolean.opBoolean","COPY",FACE,{"derivedFrom":makeQuery(id+"F49.opExtrude","SWEPT_FACE",FACE,{"disambiguationData":[OSD([sQuery(id+"F48.wireOp",EDGE,"E688.8")])]})});
            var Q19;
            Q19=makeQuery(id+"F49.boolean.opBoolean","COPY",FACE,{"derivedFrom":makeQuery(id+"F49.opExtrude","SWEPT_FACE",FACE,{"disambiguationData":[OSD([sQuery(id+"F48.wireOp",EDGE,"E688.4")])]})});
            var Q20;
            Q20=makeQuery(id+"F49.boolean.opBoolean","COPY",FACE,{"derivedFrom":makeQuery(id+"F49.opExtrude","SWEPT_FACE",FACE,{"disambiguationData":[OSD([sQuery(id+"F48.wireOp",EDGE,"E688.1")])]})});
            shell(context, id + "F50", {"entities" : qUnion([Q0, Q1, Q2, Q3, Q4, Q5, Q6, Q7, Q8, Q9, Q10, Q11, Q12, Q13, Q14, Q15, Q16, Q17, Q18, Q19, Q20]), "thickness" : 19.05 * mm});
        }
        {
            var Q0;
            {var subQ2=sQuery(id+"F5.wireOp",EDGE,"E619.1");var subQ3=sQuery(id+"F5.wireOp",EDGE,"E619.0");Q0=makeQuery(id+"F36.boolean.opBoolean","SPLIT",FACE,{"disambiguationData":[TD([makeQuery(id+"F18.opPattern","COPY",FACE,{"derivedFrom":makeQuery(id+"F17.opPattern","COPY",FACE,{"derivedFrom":makeQuery(id+"F16.opPattern","COPY",FACE,{"derivedFrom":makeQuery(id+"F15.opPattern","COPY",FACE,{"derivedFrom":makeQuery(id+"F14.opPattern","COPY",FACE,{"derivedFrom":makeQuery(id+"F6.opExtrude","SWEPT_FACE",FACE,{"disambiguationData":[OSD([subQ2])]}),"instanceName":"1"}),"instanceName":"1"}),"instanceName":"1"}),"instanceName":"1"}),"instanceName":"1"})])],"derivedFrom":makeQuery(id+"F18.opPattern","COPY",FACE,{"derivedFrom":makeQuery(id+"F17.opPattern","COPY",FACE,{"derivedFrom":makeQuery(id+"F16.opPattern","COPY",FACE,{"derivedFrom":makeQuery(id+"F15.opPattern","COPY",FACE,{"derivedFrom":makeQuery(id+"F14.opPattern","COPY",FACE,{"derivedFrom":makeQuery(id+"F6.opExtrude","SWEPT_FACE",FACE,{"disambiguationData":[OSD([subQ3])]}),"instanceName":"1"}),"instanceName":"1"}),"instanceName":"1"}),"instanceName":"1"}),"instanceName":"1"})});}
            var sketch = newSketch(context, id + "F51", { "sketchPlane" : qUnion([Q0])});
            skLineSegment(sketch, "E693.bottom", {"start": v(1275.5, -554.52) * mm, "end": v(1929.55, -554.52) * mm});
            skLineSegment(sketch, "E693.top", {"start": v(1275.5, -557.7) * mm, "end": v(1929.55, -557.7) * mm});
            skLineSegment(sketch, "E693.left", {"start": v(1275.5, -554.52) * mm, "end": v(1275.5, -557.7) * mm});
            skLineSegment(sketch, "E693.right", {"start": v(1929.55, -554.52) * mm, "end": v(1929.55, -557.7) * mm});
            skLineSegment(sketch, "E694.bottom", {"start": v(1275.5, -908.93) * mm, "end": v(1929.55, -908.93) * mm});
            skLineSegment(sketch, "E694.top", {"start": v(1275.5, -912.1) * mm, "end": v(1929.55, -912.1) * mm});
            skLineSegment(sketch, "E694.left", {"start": v(1275.5, -908.93) * mm, "end": v(1275.5, -912.1) * mm});
            skLineSegment(sketch, "E694.right", {"start": v(1929.55, -908.93) * mm, "end": v(1929.55, -912.1) * mm});
            skSolve(sketch);
        }
        {
            var Q0;
            Q0 = qSketchRegion(id + "F51", true);
            extrude(context, id + "F52", {"entities" : qUnion([Q0]), "operationType" : NewBodyOperationType.REMOVE, "oppositeDirection" : true, "depth" : 355.6 * mm});
        }
        {
            var Q0;
            {var subQ3=sQuery(id+"F3.wireOp",EDGE,"E615.2");Q0=makeQuery(id+"F23.boolean.opBoolean","SPLIT",FACE,{"disambiguationData":[TD([makeQuery(id+"F23.opExtrude","SWEPT_FACE",FACE,{"disambiguationData":[OSD([sQuery(id+"F22.wireOp",EDGE,"E646")])]})])],"derivedFrom":makeQuery(id+"F10.opPattern","COPY",FACE,{"derivedFrom":makeQuery(id+"F9.opPattern","COPY",FACE,{"derivedFrom":makeQuery(id+"F4.opExtrude","SWEPT_FACE",FACE,{"disambiguationData":[OSD([subQ3])]}),"instanceName":"1"}),"instanceName":"1"})});}
            var sketch = newSketch(context, id + "F53", { "sketchPlane" : qUnion([Q0])});
            skCircle(sketch, "E695.0", {"center": v(-620.36, 3888.25) * mm, "radius": 14 * mm});
            skLineSegment(sketch, "E696.0", {"start": v(-619.6, 3883.25) * mm, "end": v(-619.6, 3893.25) * mm});
            skLineSegment(sketch, "E696.1", {"start": v(-621.1, 3893.25) * mm, "end": v(-619.6, 3893.25) * mm});
            skLineSegment(sketch, "E696.2", {"start": v(-621.1, 3893.25) * mm, "end": v(-621.1, 3883.25) * mm});
            skLineSegment(sketch, "E696.3", {"start": v(-621.1, 3883.25) * mm, "end": v(-619.6, 3883.25) * mm});
            skSolve(sketch);
        }
        {
            var Q0;
            Q0 = qSketchRegion(id + "F53", true);
            extrude(context, id + "F54", {"entities" : qUnion([Q0]), "depth" : 19.05 * mm});
        }
        {
            var Q0;
            Q0=makeQuery(id+"F54.opExtrude","CAP_EDGE",EDGE,{"disambiguationData":[OSD([sQuery(id+"F53.wireOp",EDGE,"E695.0")])],"isStart":false});
            fillet(context, id + "F55", {"entities" : qUnion([Q0]), "radius" : 5.08 * mm, "tangentPropagation" : true, "allowEdgeOverflow" : false});
        }
    });
